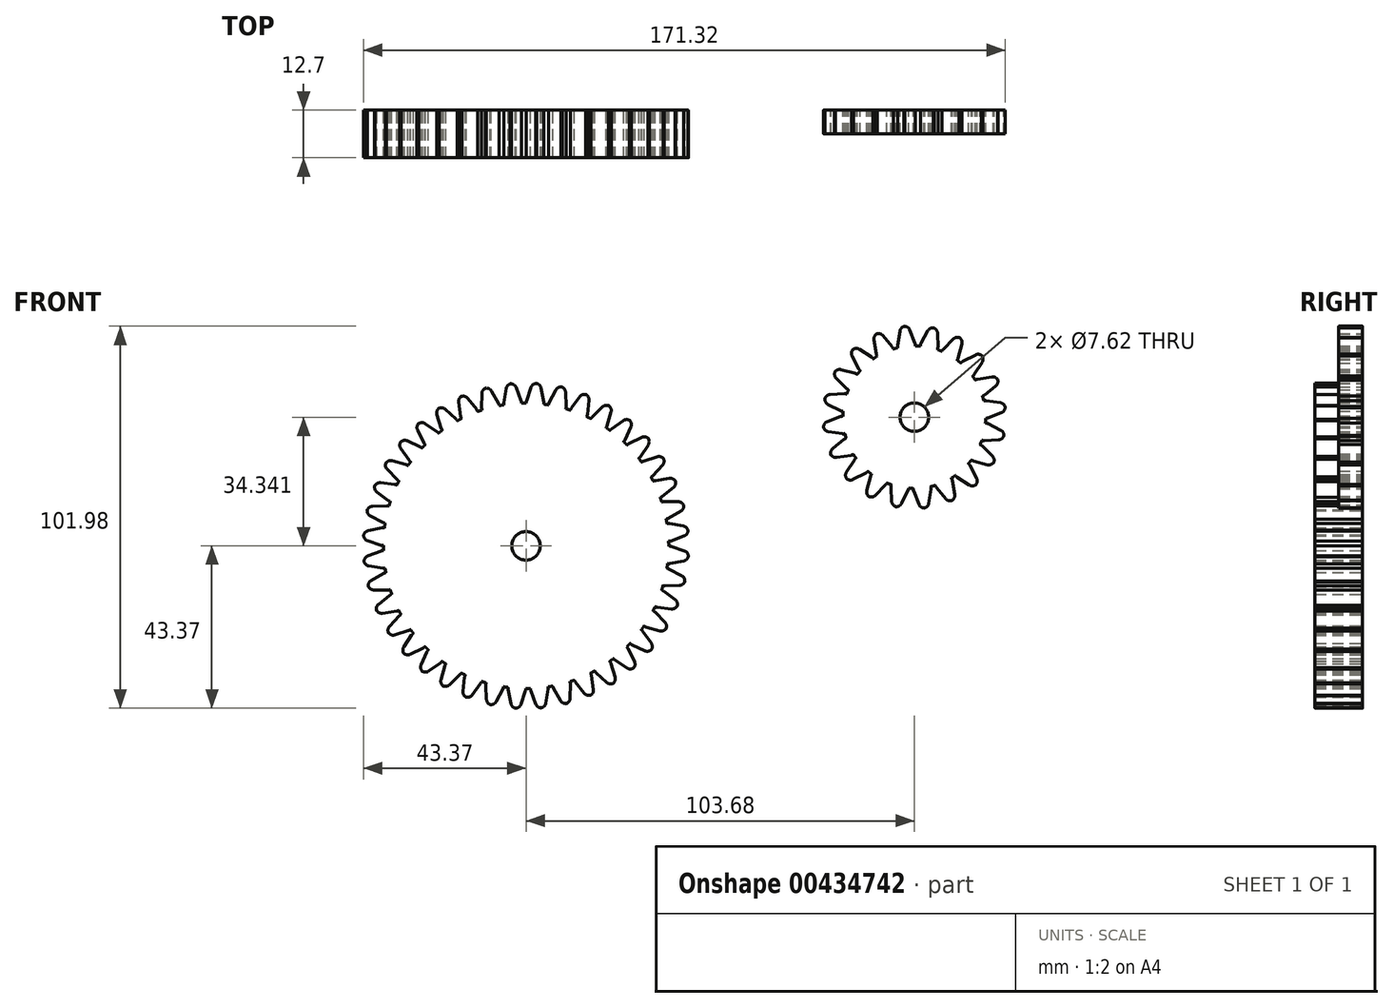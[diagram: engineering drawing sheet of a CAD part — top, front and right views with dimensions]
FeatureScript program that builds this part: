
annotation { "Feature Type Name" : "Feature", "Feature Type Description" : "" }
export const myFeature = defineFeature(function(context is Context, id is Id, definition is map)
    precondition{}
    {
        {
            var Q0;
            Q0=qCreatedBy(makeId("Front.planeOp"),FACE);
            var sketch = newSketch(context, id + "F0", { "sketchPlane" : qUnion([Q0])});
            skCircle(sketch, "E0", {"center": v(0, 0) * mm, "radius": 38.1 * mm});
            skCircle(sketch, "E1", {"center": v(103.68, 34.34) * mm, "radius": 19.05 * mm});
            skCircle(sketch, "E2", {"center": v(0, 0) * mm, "radius": 3.81 * mm});
            skCircle(sketch, "E3", {"center": v(103.68, 34.34) * mm, "radius": 3.81 * mm});
            skLineSegment(sketch, "E4.0", {"start": v(29.52, 22.13) * mm, "end": v(32.62, 17.24) * mm, "construction": true});
            skLineSegment(sketch, "E4.1", {"start": v(32.62, 17.24) * mm, "end": v(34.91, 11.93) * mm, "construction": true});
            skLineSegment(sketch, "E4.2", {"start": v(34.91, 11.93) * mm, "end": v(36.35, 6.32) * mm, "construction": true});
            skLineSegment(sketch, "E4.3", {"start": v(36.35, 6.32) * mm, "end": v(36.89, 0.56) * mm, "construction": true});
            skLineSegment(sketch, "E4.4", {"start": v(36.89, 0.56) * mm, "end": v(36.52, -5.22) * mm, "construction": true});
            skLineSegment(sketch, "E4.5", {"start": v(36.52, -5.22) * mm, "end": v(35.26, -10.87) * mm, "construction": true});
            skLineSegment(sketch, "E4.6", {"start": v(35.26, -10.87) * mm, "end": v(33.12, -16.25) * mm, "construction": true});
            skLineSegment(sketch, "E4.7", {"start": v(33.12, -16.25) * mm, "end": v(30.17, -21.23) * mm, "construction": true});
            skLineSegment(sketch, "E4.8", {"start": v(30.17, -21.23) * mm, "end": v(26.48, -25.7) * mm, "construction": true});
            skLineSegment(sketch, "E4.9", {"start": v(26.48, -25.7) * mm, "end": v(22.13, -29.52) * mm, "construction": true});
            skLineSegment(sketch, "E4.10", {"start": v(22.13, -29.52) * mm, "end": v(17.24, -32.62) * mm, "construction": true});
            skLineSegment(sketch, "E4.11", {"start": v(17.24, -32.62) * mm, "end": v(11.93, -34.91) * mm, "construction": true});
            skLineSegment(sketch, "E4.12", {"start": v(11.93, -34.91) * mm, "end": v(6.32, -36.35) * mm, "construction": true});
            skLineSegment(sketch, "E4.13", {"start": v(6.32, -36.35) * mm, "end": v(0.56, -36.89) * mm, "construction": true});
            skLineSegment(sketch, "E4.14", {"start": v(0.56, -36.89) * mm, "end": v(-5.22, -36.52) * mm, "construction": true});
            skLineSegment(sketch, "E4.15", {"start": v(-5.22, -36.52) * mm, "end": v(-10.87, -35.26) * mm, "construction": true});
            skLineSegment(sketch, "E4.16", {"start": v(-10.87, -35.26) * mm, "end": v(-16.25, -33.12) * mm, "construction": true});
            skLineSegment(sketch, "E4.17", {"start": v(-16.25, -33.12) * mm, "end": v(-21.23, -30.17) * mm, "construction": true});
            skLineSegment(sketch, "E4.18", {"start": v(-21.23, -30.17) * mm, "end": v(-25.7, -26.48) * mm, "construction": true});
            skLineSegment(sketch, "E4.19", {"start": v(-25.7, -26.48) * mm, "end": v(-29.52, -22.13) * mm, "construction": true});
            skLineSegment(sketch, "E4.20", {"start": v(-29.52, -22.13) * mm, "end": v(-32.62, -17.24) * mm, "construction": true});
            skLineSegment(sketch, "E4.21", {"start": v(-32.62, -17.24) * mm, "end": v(-34.91, -11.93) * mm, "construction": true});
            skLineSegment(sketch, "E4.22", {"start": v(-34.91, -11.93) * mm, "end": v(-36.35, -6.32) * mm, "construction": true});
            skLineSegment(sketch, "E4.23", {"start": v(-36.35, -6.32) * mm, "end": v(-36.89, -0.56) * mm, "construction": true});
            skLineSegment(sketch, "E4.24", {"start": v(-36.89, -0.56) * mm, "end": v(-36.52, 5.22) * mm, "construction": true});
            skLineSegment(sketch, "E4.25", {"start": v(-36.52, 5.22) * mm, "end": v(-35.26, 10.87) * mm, "construction": true});
            skLineSegment(sketch, "E4.26", {"start": v(-35.26, 10.87) * mm, "end": v(-33.12, 16.25) * mm, "construction": true});
            skLineSegment(sketch, "E4.27", {"start": v(-33.12, 16.25) * mm, "end": v(-30.17, 21.23) * mm, "construction": true});
            skLineSegment(sketch, "E4.28", {"start": v(-30.17, 21.23) * mm, "end": v(-26.48, 25.7) * mm, "construction": true});
            skLineSegment(sketch, "E4.29", {"start": v(-26.48, 25.7) * mm, "end": v(-22.13, 29.52) * mm, "construction": true});
            skLineSegment(sketch, "E4.30", {"start": v(-22.13, 29.52) * mm, "end": v(-17.24, 32.62) * mm, "construction": true});
            skLineSegment(sketch, "E4.31", {"start": v(-17.24, 32.62) * mm, "end": v(-11.93, 34.91) * mm, "construction": true});
            skLineSegment(sketch, "E4.32", {"start": v(-11.93, 34.91) * mm, "end": v(-6.32, 36.35) * mm, "construction": true});
            skLineSegment(sketch, "E4.33", {"start": v(-6.32, 36.35) * mm, "end": v(-0.56, 36.89) * mm, "construction": true});
            skLineSegment(sketch, "E4.34", {"start": v(-0.56, 36.89) * mm, "end": v(5.22, 36.52) * mm, "construction": true});
            skLineSegment(sketch, "E4.35", {"start": v(5.22, 36.52) * mm, "end": v(10.87, 35.26) * mm, "construction": true});
            skLineSegment(sketch, "E4.36", {"start": v(10.87, 35.26) * mm, "end": v(16.25, 33.12) * mm, "construction": true});
            skLineSegment(sketch, "E4.37", {"start": v(16.25, 33.12) * mm, "end": v(21.23, 30.17) * mm, "construction": true});
            skLineSegment(sketch, "E4.38", {"start": v(21.23, 30.17) * mm, "end": v(25.7, 26.48) * mm, "construction": true});
            skLineSegment(sketch, "E4.39", {"start": v(25.7, 26.48) * mm, "end": v(29.52, 22.13) * mm, "construction": true});
            skLineSegment(sketch, "E5", {"start": v(-17.36, 39.83) * mm, "end": v(-17.1, 39.94) * mm});
            skLineSegment(sketch, "E6", {"start": v(-15.56, 39.37) * mm, "end": v(-13.2, 36.38) * mm});
            skLineSegment(sketch, "E7", {"start": v(-13.77, 34.12) * mm, "end": v(-15.4, 33.41) * mm});
            skLineSegment(sketch, "E8", {"start": v(-17.45, 34.55) * mm, "end": v(-18, 38.32) * mm});
            skArc(sketch, "E9.filletArc", {"start": v(-17.1, 39.94) * mm, "mid": v(-17.82, 39.28) * mm, "end": v(-18, 38.32) * mm});
            skArc(sketch, "E10.filletArc", {"start": v(-15.56, 39.37) * mm, "mid": v(-16.39, 39.9) * mm, "end": v(-17.36, 39.83) * mm});
            skArc(sketch, "E11.filletArc", {"start": v(-13.77, 34.12) * mm, "mid": v(-12.92, 35.1) * mm, "end": v(-13.2, 36.38) * mm});
            skArc(sketch, "E12.filletArc", {"start": v(-17.45, 34.55) * mm, "mid": v(-16.7, 33.48) * mm, "end": v(-15.4, 33.41) * mm});
            skPoint(sketch, "E13", {"position": v(-14.59, 33.76) * mm});
            skLineSegment(sketch, "E14", {"start": v(-85, 50.08) * mm, "end": v(-84.77, 50.25) * mm});
            skLineSegment(sketch, "E15", {"start": v(-83.15, 50) * mm, "end": v(-80.23, 47.57) * mm});
            skLineSegment(sketch, "E16", {"start": v(-80.32, 45.23) * mm, "end": v(-81.77, 44.2) * mm});
            skLineSegment(sketch, "E17", {"start": v(-84, 44.9) * mm, "end": v(-85.32, 48.48) * mm});
            skArc(sketch, "E18.filletArc", {"start": v(-84.77, 50.25) * mm, "mid": v(-85.35, 49.46) * mm, "end": v(-85.32, 48.48) * mm});
            skArc(sketch, "E19.filletArc", {"start": v(-83.15, 50) * mm, "mid": v(-84.07, 50.36) * mm, "end": v(-85, 50.08) * mm});
            skArc(sketch, "E20.filletArc", {"start": v(-80.32, 45.23) * mm, "mid": v(-79.7, 46.38) * mm, "end": v(-80.23, 47.57) * mm});
            skArc(sketch, "E21.filletArc", {"start": v(-84, 44.9) * mm, "mid": v(-83.06, 44) * mm, "end": v(-81.77, 44.2) * mm});
            skPoint(sketch, "E22", {"position": v(-81.05, 44.72) * mm});
            skLineSegment(sketch, "E23", {"start": v(-94.33, 43.84) * mm, "end": v(-94.02, 44.02) * mm});
            skLineSegment(sketch, "E24", {"start": v(-92.1, 43.68) * mm, "end": v(-89.63, 40.77) * mm});
            skLineSegment(sketch, "E25", {"start": v(-90.02, 38.55) * mm, "end": v(-91.55, 37.65) * mm});
            skLineSegment(sketch, "E26", {"start": v(-93.68, 38.42) * mm, "end": v(-95, 42) * mm});
            skArc(sketch, "E27.filletArc", {"start": v(-94.33, 43.84) * mm, "mid": v(-95, 43.04) * mm, "end": v(-95, 42) * mm});
            skArc(sketch, "E28.filletArc", {"start": v(-92.1, 43.68) * mm, "mid": v(-93, 44.2) * mm, "end": v(-94.02, 44.02) * mm});
            skArc(sketch, "E29.filletArc", {"start": v(-90.02, 38.55) * mm, "mid": v(-89.3, 39.57) * mm, "end": v(-89.63, 40.77) * mm});
            skArc(sketch, "E30.filletArc", {"start": v(-93.68, 38.42) * mm, "mid": v(-92.8, 37.54) * mm, "end": v(-91.55, 37.65) * mm});
            skPoint(sketch, "E31", {"position": v(-90.78, 38.1) * mm});
            skLineSegment(sketch, "E32", {"start": v(-10.92, 42.05) * mm, "end": v(-10.64, 42.12) * mm});
            skLineSegment(sketch, "E33", {"start": v(-9.21, 41.32) * mm, "end": v(-7.34, 38) * mm});
            skLineSegment(sketch, "E34", {"start": v(-8.26, 35.85) * mm, "end": v(-9.99, 35.4) * mm});
            skLineSegment(sketch, "E35", {"start": v(-11.83, 36.85) * mm, "end": v(-11.78, 40.66) * mm});
            skArc(sketch, "E36.filletArc", {"start": v(-10.64, 42.12) * mm, "mid": v(-11.46, 41.59) * mm, "end": v(-11.78, 40.66) * mm});
            skArc(sketch, "E37.filletArc", {"start": v(-9.21, 41.32) * mm, "mid": v(-9.94, 41.98) * mm, "end": v(-10.92, 42.05) * mm});
            skArc(sketch, "E38.filletArc", {"start": v(-8.26, 35.85) * mm, "mid": v(-7.27, 36.7) * mm, "end": v(-7.34, 38) * mm});
            skArc(sketch, "E39.filletArc", {"start": v(-11.83, 36.85) * mm, "mid": v(-11.26, 35.68) * mm, "end": v(-9.99, 35.4) * mm});
            skPoint(sketch, "E40", {"position": v(-9.12, 35.63) * mm});
            skLineSegment(sketch, "E41", {"start": v(-4.2, 43.24) * mm, "end": v(-3.92, 43.27) * mm});
            skLineSegment(sketch, "E42", {"start": v(-2.63, 42.25) * mm, "end": v(-1.3, 38.68) * mm});
            skLineSegment(sketch, "E43", {"start": v(-2.55, 36.7) * mm, "end": v(-4.32, 36.54) * mm});
            skLineSegment(sketch, "E44", {"start": v(-5.91, 38.25) * mm, "end": v(-5.28, 42) * mm});
            skArc(sketch, "E45.filletArc", {"start": v(-3.92, 43.27) * mm, "mid": v(-4.81, 42.87) * mm, "end": v(-5.28, 42) * mm});
            skArc(sketch, "E46.filletArc", {"start": v(-2.63, 42.25) * mm, "mid": v(-3.25, 43.01) * mm, "end": v(-4.2, 43.24) * mm});
            skArc(sketch, "E47.filletArc", {"start": v(-2.55, 36.7) * mm, "mid": v(-1.44, 37.38) * mm, "end": v(-1.3, 38.68) * mm});
            skArc(sketch, "E48.filletArc", {"start": v(-5.91, 38.25) * mm, "mid": v(-5.54, 37) * mm, "end": v(-4.32, 36.54) * mm});
            skPoint(sketch, "E49", {"position": v(-3.44, 36.62) * mm});
            skLineSegment(sketch, "E50", {"start": v(2.61, 43.37) * mm, "end": v(2.9, 43.35) * mm});
            skLineSegment(sketch, "E51", {"start": v(4, 42.15) * mm, "end": v(4.76, 38.41) * mm});
            skLineSegment(sketch, "E52", {"start": v(3.22, 36.65) * mm, "end": v(1.45, 36.76) * mm});
            skLineSegment(sketch, "E53", {"start": v(0.14, 38.7) * mm, "end": v(1.36, 42.31) * mm});
            skArc(sketch, "E54.filletArc", {"start": v(2.9, 43.35) * mm, "mid": v(1.95, 43.1) * mm, "end": v(1.36, 42.31) * mm});
            skArc(sketch, "E55.filletArc", {"start": v(4, 42.15) * mm, "mid": v(3.52, 43) * mm, "end": v(2.61, 43.37) * mm});
            skArc(sketch, "E56.filletArc", {"start": v(3.22, 36.65) * mm, "mid": v(4.42, 37.15) * mm, "end": v(4.76, 38.41) * mm});
            skArc(sketch, "E57.filletArc", {"start": v(0.14, 38.7) * mm, "mid": v(0.31, 37.41) * mm, "end": v(1.45, 36.76) * mm});
            skPoint(sketch, "E58", {"position": v(2.33, 36.7) * mm});
            skLineSegment(sketch, "E59", {"start": v(9.36, 42.42) * mm, "end": v(9.65, 42.36) * mm});
            skLineSegment(sketch, "E60", {"start": v(10.55, 41) * mm, "end": v(10.7, 37.2) * mm});
            skLineSegment(sketch, "E61", {"start": v(8.91, 35.7) * mm, "end": v(7.18, 36.08) * mm});
            skLineSegment(sketch, "E62", {"start": v(6.2, 38.2) * mm, "end": v(7.96, 41.58) * mm});
            skArc(sketch, "E63.filletArc", {"start": v(9.65, 42.36) * mm, "mid": v(8.67, 42.26) * mm, "end": v(7.96, 41.58) * mm});
            skArc(sketch, "E64.filletArc", {"start": v(10.55, 41) * mm, "mid": v(10.2, 41.91) * mm, "end": v(9.36, 42.42) * mm});
            skArc(sketch, "E65.filletArc", {"start": v(8.91, 35.7) * mm, "mid": v(10.18, 36) * mm, "end": v(10.7, 37.2) * mm});
            skArc(sketch, "E66.filletArc", {"start": v(6.2, 38.2) * mm, "mid": v(6.16, 36.9) * mm, "end": v(7.18, 36.08) * mm});
            skPoint(sketch, "E67", {"position": v(8.05, 35.89) * mm});
            skLineSegment(sketch, "E68", {"start": v(15.88, 40.44) * mm, "end": v(16.15, 40.33) * mm});
            skLineSegment(sketch, "E69", {"start": v(16.84, 38.84) * mm, "end": v(16.4, 35.06) * mm});
            skLineSegment(sketch, "E70", {"start": v(14.39, 33.86) * mm, "end": v(12.73, 34.52) * mm});
            skLineSegment(sketch, "E71", {"start": v(12.1, 36.77) * mm, "end": v(14.37, 39.82) * mm});
            skArc(sketch, "E72.filletArc", {"start": v(16.15, 40.33) * mm, "mid": v(15.17, 40.38) * mm, "end": v(14.37, 39.82) * mm});
            skArc(sketch, "E73.filletArc", {"start": v(16.84, 38.84) * mm, "mid": v(16.63, 39.8) * mm, "end": v(15.88, 40.44) * mm});
            skArc(sketch, "E74.filletArc", {"start": v(14.39, 33.86) * mm, "mid": v(15.69, 33.97) * mm, "end": v(16.4, 35.06) * mm});
            skArc(sketch, "E75.filletArc", {"start": v(12.1, 36.77) * mm, "mid": v(11.86, 35.48) * mm, "end": v(12.73, 34.52) * mm});
            skPoint(sketch, "E76", {"position": v(13.56, 34.19) * mm});
            skLineSegment(sketch, "E77", {"start": v(22.01, 37.45) * mm, "end": v(22.26, 37.3) * mm});
            skLineSegment(sketch, "E78", {"start": v(22.7, 35.73) * mm, "end": v(21.68, 32.06) * mm});
            skLineSegment(sketch, "E79", {"start": v(19.5, 31.2) * mm, "end": v(17.98, 32.1) * mm});
            skLineSegment(sketch, "E80", {"start": v(17.7, 34.42) * mm, "end": v(20.42, 37.09) * mm});
            skArc(sketch, "E81.filletArc", {"start": v(22.26, 37.3) * mm, "mid": v(21.3, 37.5) * mm, "end": v(20.42, 37.09) * mm});
            skArc(sketch, "E82.filletArc", {"start": v(22.7, 35.73) * mm, "mid": v(22.65, 36.71) * mm, "end": v(22.01, 37.45) * mm});
            skArc(sketch, "E83.filletArc", {"start": v(19.5, 31.2) * mm, "mid": v(20.8, 31.1) * mm, "end": v(21.68, 32.06) * mm});
            skArc(sketch, "E84.filletArc", {"start": v(17.7, 34.42) * mm, "mid": v(17.26, 33.2) * mm, "end": v(17.98, 32.1) * mm});
            skPoint(sketch, "E85", {"position": v(18.74, 31.65) * mm});
            skLineSegment(sketch, "E86", {"start": v(27.6, 33.55) * mm, "end": v(27.83, 33.36) * mm});
            skLineSegment(sketch, "E87", {"start": v(28.02, 31.74) * mm, "end": v(26.43, 28.28) * mm});
            skLineSegment(sketch, "E88", {"start": v(24.15, 27.76) * mm, "end": v(22.78, 28.9) * mm});
            skLineSegment(sketch, "E89", {"start": v(22.86, 31.23) * mm, "end": v(25.97, 33.43) * mm});
            skArc(sketch, "E90.filletArc", {"start": v(27.83, 33.36) * mm, "mid": v(26.91, 33.71) * mm, "end": v(25.97, 33.43) * mm});
            skArc(sketch, "E91.filletArc", {"start": v(28.02, 31.74) * mm, "mid": v(28.12, 32.72) * mm, "end": v(27.6, 33.55) * mm});
            skArc(sketch, "E92.filletArc", {"start": v(24.15, 27.76) * mm, "mid": v(25.42, 27.46) * mm, "end": v(26.43, 28.28) * mm});
            skArc(sketch, "E93.filletArc", {"start": v(22.86, 31.23) * mm, "mid": v(22.24, 30.08) * mm, "end": v(22.78, 28.9) * mm});
            skPoint(sketch, "E94", {"position": v(23.46, 28.32) * mm});
            skLineSegment(sketch, "E95", {"start": v(32.51, 28.82) * mm, "end": v(32.7, 28.6) * mm});
            skLineSegment(sketch, "E96", {"start": v(32.64, 26.97) * mm, "end": v(30.53, 23.8) * mm});
            skLineSegment(sketch, "E97", {"start": v(28.2, 23.64) * mm, "end": v(27.02, 24.97) * mm});
            skLineSegment(sketch, "E98", {"start": v(27.47, 27.27) * mm, "end": v(30.88, 28.96) * mm});
            skArc(sketch, "E99.filletArc", {"start": v(32.7, 28.6) * mm, "mid": v(31.85, 29.09) * mm, "end": v(30.88, 28.96) * mm});
            skArc(sketch, "E100.filletArc", {"start": v(32.64, 26.97) * mm, "mid": v(32.89, 27.91) * mm, "end": v(32.51, 28.82) * mm});
            skArc(sketch, "E101.filletArc", {"start": v(28.2, 23.64) * mm, "mid": v(29.4, 23.14) * mm, "end": v(30.53, 23.8) * mm});
            skArc(sketch, "E102.filletArc", {"start": v(27.47, 27.27) * mm, "mid": v(26.68, 26.23) * mm, "end": v(27.02, 24.97) * mm});
            skPoint(sketch, "E103", {"position": v(27.6, 24.3) * mm});
            skLineSegment(sketch, "E104", {"start": v(36.62, 23.38) * mm, "end": v(36.77, 23.13) * mm});
            skLineSegment(sketch, "E105", {"start": v(36.45, 21.53) * mm, "end": v(33.87, 18.73) * mm});
            skLineSegment(sketch, "E106", {"start": v(31.54, 18.94) * mm, "end": v(30.6, 20.44) * mm});
            skLineSegment(sketch, "E107", {"start": v(31.4, 22.64) * mm, "end": v(35.03, 23.77) * mm});
            skArc(sketch, "E108.filletArc", {"start": v(36.77, 23.13) * mm, "mid": v(36.01, 23.75) * mm, "end": v(35.03, 23.77) * mm});
            skArc(sketch, "E109.filletArc", {"start": v(36.45, 21.53) * mm, "mid": v(36.85, 22.43) * mm, "end": v(36.62, 23.38) * mm});
            skArc(sketch, "E110.filletArc", {"start": v(31.54, 18.94) * mm, "mid": v(32.66, 18.26) * mm, "end": v(33.87, 18.73) * mm});
            skArc(sketch, "E111.filletArc", {"start": v(31.4, 22.64) * mm, "mid": v(30.45, 21.74) * mm, "end": v(30.6, 20.44) * mm});
            skPoint(sketch, "E112", {"position": v(31.07, 19.69) * mm});
            skLineSegment(sketch, "E113", {"start": v(39.83, 17.36) * mm, "end": v(39.94, 17.1) * mm});
            skLineSegment(sketch, "E114", {"start": v(39.37, 15.56) * mm, "end": v(36.38, 13.2) * mm});
            skLineSegment(sketch, "E115", {"start": v(34.12, 13.77) * mm, "end": v(33.41, 15.4) * mm});
            skLineSegment(sketch, "E116", {"start": v(34.55, 17.45) * mm, "end": v(38.32, 18) * mm});
            skArc(sketch, "E117.filletArc", {"start": v(39.94, 17.1) * mm, "mid": v(39.28, 17.82) * mm, "end": v(38.32, 18) * mm});
            skArc(sketch, "E118.filletArc", {"start": v(39.37, 15.56) * mm, "mid": v(39.9, 16.39) * mm, "end": v(39.83, 17.36) * mm});
            skArc(sketch, "E119.filletArc", {"start": v(34.12, 13.77) * mm, "mid": v(35.1, 12.92) * mm, "end": v(36.38, 13.2) * mm});
            skArc(sketch, "E120.filletArc", {"start": v(34.55, 17.45) * mm, "mid": v(33.48, 16.7) * mm, "end": v(33.41, 15.4) * mm});
            skPoint(sketch, "E121", {"position": v(33.76, 14.59) * mm});
            skLineSegment(sketch, "E122", {"start": v(42.05, 10.92) * mm, "end": v(42.12, 10.64) * mm});
            skLineSegment(sketch, "E123", {"start": v(41.32, 9.21) * mm, "end": v(38, 7.34) * mm});
            skLineSegment(sketch, "E124", {"start": v(35.85, 8.26) * mm, "end": v(35.4, 9.99) * mm});
            skLineSegment(sketch, "E125", {"start": v(36.85, 11.83) * mm, "end": v(40.66, 11.78) * mm});
            skArc(sketch, "E126.filletArc", {"start": v(42.12, 10.64) * mm, "mid": v(41.59, 11.46) * mm, "end": v(40.66, 11.78) * mm});
            skArc(sketch, "E127.filletArc", {"start": v(41.32, 9.21) * mm, "mid": v(41.98, 9.94) * mm, "end": v(42.05, 10.92) * mm});
            skArc(sketch, "E128.filletArc", {"start": v(35.85, 8.26) * mm, "mid": v(36.7, 7.27) * mm, "end": v(38, 7.34) * mm});
            skArc(sketch, "E129.filletArc", {"start": v(36.85, 11.83) * mm, "mid": v(35.68, 11.26) * mm, "end": v(35.4, 9.99) * mm});
            skPoint(sketch, "E130", {"position": v(35.63, 9.12) * mm});
            skLineSegment(sketch, "E131", {"start": v(43.24, 4.2) * mm, "end": v(43.27, 3.92) * mm});
            skLineSegment(sketch, "E132", {"start": v(42.25, 2.63) * mm, "end": v(38.68, 1.3) * mm});
            skLineSegment(sketch, "E133", {"start": v(36.7, 2.55) * mm, "end": v(36.54, 4.32) * mm});
            skLineSegment(sketch, "E134", {"start": v(38.25, 5.91) * mm, "end": v(42, 5.28) * mm});
            skArc(sketch, "E135.filletArc", {"start": v(43.27, 3.92) * mm, "mid": v(42.87, 4.81) * mm, "end": v(42, 5.28) * mm});
            skArc(sketch, "E136.filletArc", {"start": v(42.25, 2.63) * mm, "mid": v(43.01, 3.25) * mm, "end": v(43.24, 4.2) * mm});
            skArc(sketch, "E137.filletArc", {"start": v(36.7, 2.55) * mm, "mid": v(37.38, 1.44) * mm, "end": v(38.68, 1.3) * mm});
            skArc(sketch, "E138.filletArc", {"start": v(38.25, 5.91) * mm, "mid": v(37, 5.54) * mm, "end": v(36.54, 4.32) * mm});
            skPoint(sketch, "E139", {"position": v(36.62, 3.44) * mm});
            skLineSegment(sketch, "E140", {"start": v(43.37, -2.61) * mm, "end": v(43.35, -2.9) * mm});
            skLineSegment(sketch, "E141", {"start": v(42.15, -4) * mm, "end": v(38.41, -4.76) * mm});
            skLineSegment(sketch, "E142", {"start": v(36.65, -3.22) * mm, "end": v(36.76, -1.45) * mm});
            skLineSegment(sketch, "E143", {"start": v(38.7, -0.14) * mm, "end": v(42.31, -1.36) * mm});
            skArc(sketch, "E144.filletArc", {"start": v(43.35, -2.9) * mm, "mid": v(43.1, -1.95) * mm, "end": v(42.31, -1.36) * mm});
            skArc(sketch, "E145.filletArc", {"start": v(42.15, -4) * mm, "mid": v(43, -3.52) * mm, "end": v(43.37, -2.61) * mm});
            skArc(sketch, "E146.filletArc", {"start": v(36.65, -3.22) * mm, "mid": v(37.15, -4.42) * mm, "end": v(38.41, -4.76) * mm});
            skArc(sketch, "E147.filletArc", {"start": v(38.7, -0.14) * mm, "mid": v(37.41, -0.31) * mm, "end": v(36.76, -1.45) * mm});
            skPoint(sketch, "E148", {"position": v(36.7, -2.33) * mm});
            skLineSegment(sketch, "E149", {"start": v(42.42, -9.36) * mm, "end": v(42.36, -9.65) * mm});
            skLineSegment(sketch, "E150", {"start": v(41, -10.55) * mm, "end": v(37.2, -10.7) * mm});
            skLineSegment(sketch, "E151", {"start": v(35.7, -8.91) * mm, "end": v(36.08, -7.18) * mm});
            skLineSegment(sketch, "E152", {"start": v(38.2, -6.2) * mm, "end": v(41.58, -7.96) * mm});
            skArc(sketch, "E153.filletArc", {"start": v(42.36, -9.65) * mm, "mid": v(42.26, -8.67) * mm, "end": v(41.58, -7.96) * mm});
            skArc(sketch, "E154.filletArc", {"start": v(41, -10.55) * mm, "mid": v(41.91, -10.2) * mm, "end": v(42.42, -9.36) * mm});
            skArc(sketch, "E155.filletArc", {"start": v(35.7, -8.91) * mm, "mid": v(36, -10.18) * mm, "end": v(37.2, -10.7) * mm});
            skArc(sketch, "E156.filletArc", {"start": v(38.2, -6.2) * mm, "mid": v(36.9, -6.16) * mm, "end": v(36.08, -7.18) * mm});
            skPoint(sketch, "E157", {"position": v(35.89, -8.05) * mm});
            skLineSegment(sketch, "E158", {"start": v(40.44, -15.88) * mm, "end": v(40.33, -16.15) * mm});
            skLineSegment(sketch, "E159", {"start": v(38.84, -16.84) * mm, "end": v(35.06, -16.4) * mm});
            skLineSegment(sketch, "E160", {"start": v(33.86, -14.39) * mm, "end": v(34.52, -12.73) * mm});
            skLineSegment(sketch, "E161", {"start": v(36.77, -12.1) * mm, "end": v(39.82, -14.37) * mm});
            skArc(sketch, "E162.filletArc", {"start": v(40.33, -16.15) * mm, "mid": v(40.38, -15.17) * mm, "end": v(39.82, -14.37) * mm});
            skArc(sketch, "E163.filletArc", {"start": v(38.84, -16.84) * mm, "mid": v(39.8, -16.63) * mm, "end": v(40.44, -15.88) * mm});
            skArc(sketch, "E164.filletArc", {"start": v(33.86, -14.39) * mm, "mid": v(33.97, -15.69) * mm, "end": v(35.06, -16.4) * mm});
            skArc(sketch, "E165.filletArc", {"start": v(36.77, -12.1) * mm, "mid": v(35.48, -11.86) * mm, "end": v(34.52, -12.73) * mm});
            skPoint(sketch, "E166", {"position": v(34.19, -13.56) * mm});
            skLineSegment(sketch, "E167", {"start": v(37.45, -22.01) * mm, "end": v(37.3, -22.26) * mm});
            skLineSegment(sketch, "E168", {"start": v(35.73, -22.7) * mm, "end": v(32.06, -21.68) * mm});
            skLineSegment(sketch, "E169", {"start": v(31.2, -19.5) * mm, "end": v(32.1, -17.98) * mm});
            skLineSegment(sketch, "E170", {"start": v(34.42, -17.7) * mm, "end": v(37.09, -20.42) * mm});
            skArc(sketch, "E171.filletArc", {"start": v(37.3, -22.26) * mm, "mid": v(37.5, -21.3) * mm, "end": v(37.09, -20.42) * mm});
            skArc(sketch, "E172.filletArc", {"start": v(35.73, -22.7) * mm, "mid": v(36.71, -22.65) * mm, "end": v(37.45, -22.01) * mm});
            skArc(sketch, "E173.filletArc", {"start": v(31.2, -19.5) * mm, "mid": v(31.1, -20.8) * mm, "end": v(32.06, -21.68) * mm});
            skArc(sketch, "E174.filletArc", {"start": v(34.42, -17.7) * mm, "mid": v(33.2, -17.26) * mm, "end": v(32.1, -17.98) * mm});
            skPoint(sketch, "E175", {"position": v(31.65, -18.74) * mm});
            skLineSegment(sketch, "E176", {"start": v(33.55, -27.6) * mm, "end": v(33.36, -27.83) * mm});
            skLineSegment(sketch, "E177", {"start": v(31.74, -28.02) * mm, "end": v(28.28, -26.43) * mm});
            skLineSegment(sketch, "E178", {"start": v(27.76, -24.15) * mm, "end": v(28.9, -22.78) * mm});
            skLineSegment(sketch, "E179", {"start": v(31.23, -22.86) * mm, "end": v(33.43, -25.97) * mm});
            skArc(sketch, "E180.filletArc", {"start": v(33.36, -27.83) * mm, "mid": v(33.71, -26.91) * mm, "end": v(33.43, -25.97) * mm});
            skArc(sketch, "E181.filletArc", {"start": v(31.74, -28.02) * mm, "mid": v(32.72, -28.12) * mm, "end": v(33.55, -27.6) * mm});
            skArc(sketch, "E182.filletArc", {"start": v(27.76, -24.15) * mm, "mid": v(27.46, -25.42) * mm, "end": v(28.28, -26.43) * mm});
            skArc(sketch, "E183.filletArc", {"start": v(31.23, -22.86) * mm, "mid": v(30.08, -22.24) * mm, "end": v(28.9, -22.78) * mm});
            skPoint(sketch, "E184", {"position": v(28.32, -23.46) * mm});
            skLineSegment(sketch, "E185", {"start": v(28.82, -32.51) * mm, "end": v(28.6, -32.7) * mm});
            skLineSegment(sketch, "E186", {"start": v(26.97, -32.64) * mm, "end": v(23.8, -30.53) * mm});
            skLineSegment(sketch, "E187", {"start": v(23.64, -28.2) * mm, "end": v(24.97, -27.02) * mm});
            skLineSegment(sketch, "E188", {"start": v(27.27, -27.47) * mm, "end": v(28.96, -30.88) * mm});
            skArc(sketch, "E189.filletArc", {"start": v(28.6, -32.7) * mm, "mid": v(29.09, -31.85) * mm, "end": v(28.96, -30.88) * mm});
            skArc(sketch, "E190.filletArc", {"start": v(26.97, -32.64) * mm, "mid": v(27.91, -32.89) * mm, "end": v(28.82, -32.51) * mm});
            skArc(sketch, "E191.filletArc", {"start": v(23.64, -28.2) * mm, "mid": v(23.14, -29.4) * mm, "end": v(23.8, -30.53) * mm});
            skArc(sketch, "E192.filletArc", {"start": v(27.27, -27.47) * mm, "mid": v(26.23, -26.68) * mm, "end": v(24.97, -27.02) * mm});
            skPoint(sketch, "E193", {"position": v(24.3, -27.6) * mm});
            skLineSegment(sketch, "E194", {"start": v(23.38, -36.62) * mm, "end": v(23.13, -36.77) * mm});
            skLineSegment(sketch, "E195", {"start": v(21.53, -36.45) * mm, "end": v(18.73, -33.87) * mm});
            skLineSegment(sketch, "E196", {"start": v(18.94, -31.54) * mm, "end": v(20.44, -30.6) * mm});
            skLineSegment(sketch, "E197", {"start": v(22.64, -31.4) * mm, "end": v(23.77, -35.03) * mm});
            skArc(sketch, "E198.filletArc", {"start": v(23.13, -36.77) * mm, "mid": v(23.75, -36.01) * mm, "end": v(23.77, -35.03) * mm});
            skArc(sketch, "E199.filletArc", {"start": v(21.53, -36.45) * mm, "mid": v(22.43, -36.85) * mm, "end": v(23.38, -36.62) * mm});
            skArc(sketch, "E200.filletArc", {"start": v(18.94, -31.54) * mm, "mid": v(18.26, -32.66) * mm, "end": v(18.73, -33.87) * mm});
            skArc(sketch, "E201.filletArc", {"start": v(22.64, -31.4) * mm, "mid": v(21.74, -30.45) * mm, "end": v(20.44, -30.6) * mm});
            skPoint(sketch, "E202", {"position": v(19.69, -31.07) * mm});
            skLineSegment(sketch, "E203", {"start": v(4.2, -43.24) * mm, "end": v(3.92, -43.27) * mm});
            skLineSegment(sketch, "E204", {"start": v(2.63, -42.25) * mm, "end": v(1.3, -38.68) * mm});
            skLineSegment(sketch, "E205", {"start": v(2.55, -36.7) * mm, "end": v(4.32, -36.54) * mm});
            skLineSegment(sketch, "E206", {"start": v(5.91, -38.25) * mm, "end": v(5.28, -42) * mm});
            skArc(sketch, "E207.filletArc", {"start": v(3.92, -43.27) * mm, "mid": v(4.81, -42.87) * mm, "end": v(5.28, -42) * mm});
            skArc(sketch, "E208.filletArc", {"start": v(2.63, -42.25) * mm, "mid": v(3.25, -43.01) * mm, "end": v(4.2, -43.24) * mm});
            skArc(sketch, "E209.filletArc", {"start": v(2.55, -36.7) * mm, "mid": v(1.44, -37.38) * mm, "end": v(1.3, -38.68) * mm});
            skArc(sketch, "E210.filletArc", {"start": v(5.91, -38.25) * mm, "mid": v(5.54, -37) * mm, "end": v(4.32, -36.54) * mm});
            skPoint(sketch, "E211", {"position": v(3.44, -36.62) * mm});
            skLineSegment(sketch, "E212", {"start": v(10.92, -42.05) * mm, "end": v(10.64, -42.12) * mm});
            skLineSegment(sketch, "E213", {"start": v(9.21, -41.32) * mm, "end": v(7.34, -38) * mm});
            skLineSegment(sketch, "E214", {"start": v(8.26, -35.85) * mm, "end": v(9.99, -35.4) * mm});
            skLineSegment(sketch, "E215", {"start": v(11.83, -36.85) * mm, "end": v(11.78, -40.66) * mm});
            skArc(sketch, "E216.filletArc", {"start": v(10.64, -42.12) * mm, "mid": v(11.46, -41.59) * mm, "end": v(11.78, -40.66) * mm});
            skArc(sketch, "E217.filletArc", {"start": v(9.21, -41.32) * mm, "mid": v(9.94, -41.98) * mm, "end": v(10.92, -42.05) * mm});
            skArc(sketch, "E218.filletArc", {"start": v(8.26, -35.85) * mm, "mid": v(7.27, -36.7) * mm, "end": v(7.34, -38) * mm});
            skArc(sketch, "E219.filletArc", {"start": v(11.83, -36.85) * mm, "mid": v(11.26, -35.68) * mm, "end": v(9.99, -35.4) * mm});
            skPoint(sketch, "E220", {"position": v(9.12, -35.63) * mm});
            skLineSegment(sketch, "E221", {"start": v(17.36, -39.83) * mm, "end": v(17.1, -39.94) * mm});
            skLineSegment(sketch, "E222", {"start": v(15.56, -39.37) * mm, "end": v(13.2, -36.38) * mm});
            skLineSegment(sketch, "E223", {"start": v(13.77, -34.12) * mm, "end": v(15.4, -33.41) * mm});
            skLineSegment(sketch, "E224", {"start": v(17.45, -34.55) * mm, "end": v(18, -38.32) * mm});
            skArc(sketch, "E225.filletArc", {"start": v(17.1, -39.94) * mm, "mid": v(17.82, -39.28) * mm, "end": v(18, -38.32) * mm});
            skArc(sketch, "E226.filletArc", {"start": v(15.56, -39.37) * mm, "mid": v(16.39, -39.9) * mm, "end": v(17.36, -39.83) * mm});
            skArc(sketch, "E227.filletArc", {"start": v(13.77, -34.12) * mm, "mid": v(12.92, -35.1) * mm, "end": v(13.2, -36.38) * mm});
            skArc(sketch, "E228.filletArc", {"start": v(17.45, -34.55) * mm, "mid": v(16.7, -33.48) * mm, "end": v(15.4, -33.41) * mm});
            skPoint(sketch, "E229", {"position": v(14.59, -33.76) * mm});
            skLineSegment(sketch, "E230", {"start": v(-2.61, -43.37) * mm, "end": v(-2.9, -43.35) * mm});
            skLineSegment(sketch, "E231", {"start": v(-4, -42.15) * mm, "end": v(-4.76, -38.41) * mm});
            skLineSegment(sketch, "E232", {"start": v(-3.22, -36.65) * mm, "end": v(-1.45, -36.76) * mm});
            skLineSegment(sketch, "E233", {"start": v(-0.14, -38.7) * mm, "end": v(-1.36, -42.31) * mm});
            skArc(sketch, "E234.filletArc", {"start": v(-2.9, -43.35) * mm, "mid": v(-1.95, -43.1) * mm, "end": v(-1.36, -42.31) * mm});
            skArc(sketch, "E235.filletArc", {"start": v(-4, -42.15) * mm, "mid": v(-3.52, -43) * mm, "end": v(-2.61, -43.37) * mm});
            skArc(sketch, "E236.filletArc", {"start": v(-3.22, -36.65) * mm, "mid": v(-4.42, -37.15) * mm, "end": v(-4.76, -38.41) * mm});
            skArc(sketch, "E237.filletArc", {"start": v(-0.14, -38.7) * mm, "mid": v(-0.31, -37.41) * mm, "end": v(-1.45, -36.76) * mm});
            skPoint(sketch, "E238", {"position": v(-2.33, -36.7) * mm});
            skLineSegment(sketch, "E239", {"start": v(-9.36, -42.42) * mm, "end": v(-9.65, -42.36) * mm});
            skLineSegment(sketch, "E240", {"start": v(-10.55, -41) * mm, "end": v(-10.7, -37.2) * mm});
            skLineSegment(sketch, "E241", {"start": v(-8.91, -35.7) * mm, "end": v(-7.18, -36.08) * mm});
            skLineSegment(sketch, "E242", {"start": v(-6.2, -38.2) * mm, "end": v(-7.96, -41.58) * mm});
            skArc(sketch, "E243.filletArc", {"start": v(-9.65, -42.36) * mm, "mid": v(-8.67, -42.26) * mm, "end": v(-7.96, -41.58) * mm});
            skArc(sketch, "E244.filletArc", {"start": v(-10.55, -41) * mm, "mid": v(-10.2, -41.91) * mm, "end": v(-9.36, -42.42) * mm});
            skArc(sketch, "E245.filletArc", {"start": v(-8.91, -35.7) * mm, "mid": v(-10.18, -36) * mm, "end": v(-10.7, -37.2) * mm});
            skArc(sketch, "E246.filletArc", {"start": v(-6.2, -38.2) * mm, "mid": v(-6.16, -36.9) * mm, "end": v(-7.18, -36.08) * mm});
            skPoint(sketch, "E247", {"position": v(-8.05, -35.89) * mm});
            skLineSegment(sketch, "E248", {"start": v(-15.88, -40.44) * mm, "end": v(-16.15, -40.33) * mm});
            skLineSegment(sketch, "E249", {"start": v(-16.84, -38.84) * mm, "end": v(-16.4, -35.06) * mm});
            skLineSegment(sketch, "E250", {"start": v(-14.39, -33.86) * mm, "end": v(-12.73, -34.52) * mm});
            skLineSegment(sketch, "E251", {"start": v(-12.1, -36.77) * mm, "end": v(-14.37, -39.82) * mm});
            skArc(sketch, "E252.filletArc", {"start": v(-16.15, -40.33) * mm, "mid": v(-15.17, -40.38) * mm, "end": v(-14.37, -39.82) * mm});
            skArc(sketch, "E253.filletArc", {"start": v(-16.84, -38.84) * mm, "mid": v(-16.63, -39.8) * mm, "end": v(-15.88, -40.44) * mm});
            skArc(sketch, "E254.filletArc", {"start": v(-14.39, -33.86) * mm, "mid": v(-15.69, -33.97) * mm, "end": v(-16.4, -35.06) * mm});
            skArc(sketch, "E255.filletArc", {"start": v(-12.1, -36.77) * mm, "mid": v(-11.86, -35.48) * mm, "end": v(-12.73, -34.52) * mm});
            skPoint(sketch, "E256", {"position": v(-13.56, -34.19) * mm});
            skLineSegment(sketch, "E257", {"start": v(-22.01, -37.45) * mm, "end": v(-22.26, -37.3) * mm});
            skLineSegment(sketch, "E258", {"start": v(-22.7, -35.73) * mm, "end": v(-21.68, -32.06) * mm});
            skLineSegment(sketch, "E259", {"start": v(-19.5, -31.2) * mm, "end": v(-17.98, -32.1) * mm});
            skLineSegment(sketch, "E260", {"start": v(-17.7, -34.42) * mm, "end": v(-20.42, -37.09) * mm});
            skArc(sketch, "E261.filletArc", {"start": v(-22.26, -37.3) * mm, "mid": v(-21.3, -37.5) * mm, "end": v(-20.42, -37.09) * mm});
            skArc(sketch, "E262.filletArc", {"start": v(-22.7, -35.73) * mm, "mid": v(-22.65, -36.71) * mm, "end": v(-22.01, -37.45) * mm});
            skArc(sketch, "E263.filletArc", {"start": v(-19.5, -31.2) * mm, "mid": v(-20.8, -31.1) * mm, "end": v(-21.68, -32.06) * mm});
            skArc(sketch, "E264.filletArc", {"start": v(-17.7, -34.42) * mm, "mid": v(-17.26, -33.2) * mm, "end": v(-17.98, -32.1) * mm});
            skPoint(sketch, "E265", {"position": v(-18.74, -31.65) * mm});
            skLineSegment(sketch, "E266", {"start": v(-27.6, -33.55) * mm, "end": v(-27.83, -33.36) * mm});
            skLineSegment(sketch, "E267", {"start": v(-28.02, -31.74) * mm, "end": v(-26.43, -28.28) * mm});
            skLineSegment(sketch, "E268", {"start": v(-24.15, -27.76) * mm, "end": v(-22.78, -28.9) * mm});
            skLineSegment(sketch, "E269", {"start": v(-22.86, -31.23) * mm, "end": v(-25.97, -33.43) * mm});
            skArc(sketch, "E270.filletArc", {"start": v(-27.83, -33.36) * mm, "mid": v(-26.91, -33.71) * mm, "end": v(-25.97, -33.43) * mm});
            skArc(sketch, "E271.filletArc", {"start": v(-28.02, -31.74) * mm, "mid": v(-28.12, -32.72) * mm, "end": v(-27.6, -33.55) * mm});
            skArc(sketch, "E272.filletArc", {"start": v(-24.15, -27.76) * mm, "mid": v(-25.42, -27.46) * mm, "end": v(-26.43, -28.28) * mm});
            skArc(sketch, "E273.filletArc", {"start": v(-22.86, -31.23) * mm, "mid": v(-22.24, -30.08) * mm, "end": v(-22.78, -28.9) * mm});
            skPoint(sketch, "E274", {"position": v(-23.46, -28.32) * mm});
            skLineSegment(sketch, "E275", {"start": v(-32.51, -28.82) * mm, "end": v(-32.7, -28.6) * mm});
            skLineSegment(sketch, "E276", {"start": v(-32.64, -26.97) * mm, "end": v(-30.53, -23.8) * mm});
            skLineSegment(sketch, "E277", {"start": v(-28.2, -23.64) * mm, "end": v(-27.02, -24.97) * mm});
            skLineSegment(sketch, "E278", {"start": v(-27.47, -27.27) * mm, "end": v(-30.88, -28.96) * mm});
            skArc(sketch, "E279.filletArc", {"start": v(-32.7, -28.6) * mm, "mid": v(-31.85, -29.09) * mm, "end": v(-30.88, -28.96) * mm});
            skArc(sketch, "E280.filletArc", {"start": v(-32.64, -26.97) * mm, "mid": v(-32.89, -27.91) * mm, "end": v(-32.51, -28.82) * mm});
            skArc(sketch, "E281.filletArc", {"start": v(-28.2, -23.64) * mm, "mid": v(-29.4, -23.14) * mm, "end": v(-30.53, -23.8) * mm});
            skArc(sketch, "E282.filletArc", {"start": v(-27.47, -27.27) * mm, "mid": v(-26.68, -26.23) * mm, "end": v(-27.02, -24.97) * mm});
            skPoint(sketch, "E283", {"position": v(-27.6, -24.3) * mm});
            skLineSegment(sketch, "E284", {"start": v(-39.83, -17.36) * mm, "end": v(-39.94, -17.1) * mm});
            skLineSegment(sketch, "E285", {"start": v(-39.37, -15.56) * mm, "end": v(-36.38, -13.2) * mm});
            skLineSegment(sketch, "E286", {"start": v(-34.12, -13.77) * mm, "end": v(-33.41, -15.4) * mm});
            skLineSegment(sketch, "E287", {"start": v(-34.55, -17.45) * mm, "end": v(-38.32, -18) * mm});
            skArc(sketch, "E288.filletArc", {"start": v(-39.94, -17.1) * mm, "mid": v(-39.28, -17.82) * mm, "end": v(-38.32, -18) * mm});
            skArc(sketch, "E289.filletArc", {"start": v(-39.37, -15.56) * mm, "mid": v(-39.9, -16.39) * mm, "end": v(-39.83, -17.36) * mm});
            skArc(sketch, "E290.filletArc", {"start": v(-34.12, -13.77) * mm, "mid": v(-35.1, -12.92) * mm, "end": v(-36.38, -13.2) * mm});
            skArc(sketch, "E291.filletArc", {"start": v(-34.55, -17.45) * mm, "mid": v(-33.48, -16.7) * mm, "end": v(-33.41, -15.4) * mm});
            skPoint(sketch, "E292", {"position": v(-33.76, -14.59) * mm});
            skLineSegment(sketch, "E293", {"start": v(-43.23, -4.32) * mm, "end": v(-43.26, -4.03) * mm});
            skLineSegment(sketch, "E294", {"start": v(-42.27, -2.73) * mm, "end": v(-38.72, -1.34) * mm});
            skLineSegment(sketch, "E295", {"start": v(-36.72, -2.55) * mm, "end": v(-36.52, -4.32) * mm});
            skLineSegment(sketch, "E296", {"start": v(-38.2, -5.94) * mm, "end": v(-41.97, -5.37) * mm});
            skArc(sketch, "E297.filletArc", {"start": v(-43.26, -4.03) * mm, "mid": v(-42.84, -4.92) * mm, "end": v(-41.97, -5.37) * mm});
            skArc(sketch, "E298.filletArc", {"start": v(-42.27, -2.73) * mm, "mid": v(-43.02, -3.36) * mm, "end": v(-43.23, -4.32) * mm});
            skArc(sketch, "E299.filletArc", {"start": v(-36.72, -2.55) * mm, "mid": v(-37.42, -1.46) * mm, "end": v(-38.72, -1.34) * mm});
            skArc(sketch, "E300.filletArc", {"start": v(-38.2, -5.94) * mm, "mid": v(-36.96, -5.55) * mm, "end": v(-36.52, -4.32) * mm});
            skPoint(sketch, "E301", {"position": v(-36.62, -3.44) * mm});
            skLineSegment(sketch, "E302", {"start": v(-42.05, -10.92) * mm, "end": v(-42.12, -10.64) * mm});
            skLineSegment(sketch, "E303", {"start": v(-41.32, -9.21) * mm, "end": v(-38, -7.34) * mm});
            skLineSegment(sketch, "E304", {"start": v(-35.85, -8.26) * mm, "end": v(-35.4, -9.99) * mm});
            skLineSegment(sketch, "E305", {"start": v(-36.85, -11.83) * mm, "end": v(-40.66, -11.78) * mm});
            skArc(sketch, "E306.filletArc", {"start": v(-42.12, -10.64) * mm, "mid": v(-41.59, -11.46) * mm, "end": v(-40.66, -11.78) * mm});
            skArc(sketch, "E307.filletArc", {"start": v(-41.32, -9.21) * mm, "mid": v(-41.98, -9.94) * mm, "end": v(-42.05, -10.92) * mm});
            skArc(sketch, "E308.filletArc", {"start": v(-35.85, -8.26) * mm, "mid": v(-36.7, -7.27) * mm, "end": v(-38, -7.34) * mm});
            skArc(sketch, "E309.filletArc", {"start": v(-36.85, -11.83) * mm, "mid": v(-35.68, -11.26) * mm, "end": v(-35.4, -9.99) * mm});
            skPoint(sketch, "E310", {"position": v(-35.63, -9.12) * mm});
            skLineSegment(sketch, "E311", {"start": v(-36.62, -23.38) * mm, "end": v(-36.77, -23.13) * mm});
            skLineSegment(sketch, "E312", {"start": v(-36.45, -21.53) * mm, "end": v(-33.87, -18.73) * mm});
            skLineSegment(sketch, "E313", {"start": v(-31.54, -18.94) * mm, "end": v(-30.6, -20.44) * mm});
            skLineSegment(sketch, "E314", {"start": v(-31.4, -22.64) * mm, "end": v(-35.03, -23.77) * mm});
            skArc(sketch, "E315.filletArc", {"start": v(-36.77, -23.13) * mm, "mid": v(-36.01, -23.75) * mm, "end": v(-35.03, -23.77) * mm});
            skArc(sketch, "E316.filletArc", {"start": v(-36.45, -21.53) * mm, "mid": v(-36.85, -22.43) * mm, "end": v(-36.62, -23.38) * mm});
            skArc(sketch, "E317.filletArc", {"start": v(-31.54, -18.94) * mm, "mid": v(-32.66, -18.26) * mm, "end": v(-33.87, -18.73) * mm});
            skArc(sketch, "E318.filletArc", {"start": v(-31.4, -22.64) * mm, "mid": v(-30.45, -21.74) * mm, "end": v(-30.6, -20.44) * mm});
            skPoint(sketch, "E319", {"position": v(-31.07, -19.69) * mm});
            skLineSegment(sketch, "E320", {"start": v(-37.45, 22.01) * mm, "end": v(-37.3, 22.26) * mm});
            skLineSegment(sketch, "E321", {"start": v(-35.73, 22.7) * mm, "end": v(-32.06, 21.68) * mm});
            skLineSegment(sketch, "E322", {"start": v(-31.2, 19.5) * mm, "end": v(-32.1, 17.98) * mm});
            skLineSegment(sketch, "E323", {"start": v(-34.42, 17.7) * mm, "end": v(-37.09, 20.42) * mm});
            skArc(sketch, "E324.filletArc", {"start": v(-37.3, 22.26) * mm, "mid": v(-37.5, 21.3) * mm, "end": v(-37.09, 20.42) * mm});
            skArc(sketch, "E325.filletArc", {"start": v(-35.73, 22.7) * mm, "mid": v(-36.71, 22.65) * mm, "end": v(-37.45, 22.01) * mm});
            skArc(sketch, "E326.filletArc", {"start": v(-31.2, 19.5) * mm, "mid": v(-31.1, 20.8) * mm, "end": v(-32.06, 21.68) * mm});
            skArc(sketch, "E327.filletArc", {"start": v(-34.42, 17.7) * mm, "mid": v(-33.2, 17.26) * mm, "end": v(-32.1, 17.98) * mm});
            skPoint(sketch, "E328", {"position": v(-31.65, 18.74) * mm});
            skLineSegment(sketch, "E329", {"start": v(-42.42, 9.36) * mm, "end": v(-42.36, 9.65) * mm});
            skLineSegment(sketch, "E330", {"start": v(-41, 10.55) * mm, "end": v(-37.2, 10.7) * mm});
            skLineSegment(sketch, "E331", {"start": v(-35.7, 8.91) * mm, "end": v(-36.08, 7.18) * mm});
            skLineSegment(sketch, "E332", {"start": v(-38.2, 6.2) * mm, "end": v(-41.58, 7.96) * mm});
            skArc(sketch, "E333.filletArc", {"start": v(-42.36, 9.65) * mm, "mid": v(-42.26, 8.67) * mm, "end": v(-41.58, 7.96) * mm});
            skArc(sketch, "E334.filletArc", {"start": v(-41, 10.55) * mm, "mid": v(-41.91, 10.2) * mm, "end": v(-42.42, 9.36) * mm});
            skArc(sketch, "E335.filletArc", {"start": v(-35.7, 8.91) * mm, "mid": v(-36, 10.18) * mm, "end": v(-37.2, 10.7) * mm});
            skArc(sketch, "E336.filletArc", {"start": v(-38.2, 6.2) * mm, "mid": v(-36.9, 6.16) * mm, "end": v(-36.08, 7.18) * mm});
            skPoint(sketch, "E337", {"position": v(-35.89, 8.05) * mm});
            skLineSegment(sketch, "E338", {"start": v(-28.82, 32.51) * mm, "end": v(-28.6, 32.7) * mm});
            skLineSegment(sketch, "E339", {"start": v(-26.97, 32.64) * mm, "end": v(-23.8, 30.53) * mm});
            skLineSegment(sketch, "E340", {"start": v(-23.64, 28.2) * mm, "end": v(-24.97, 27.02) * mm});
            skLineSegment(sketch, "E341", {"start": v(-27.27, 27.47) * mm, "end": v(-28.96, 30.88) * mm});
            skArc(sketch, "E342.filletArc", {"start": v(-28.6, 32.7) * mm, "mid": v(-29.09, 31.85) * mm, "end": v(-28.96, 30.88) * mm});
            skArc(sketch, "E343.filletArc", {"start": v(-26.97, 32.64) * mm, "mid": v(-27.91, 32.89) * mm, "end": v(-28.82, 32.51) * mm});
            skArc(sketch, "E344.filletArc", {"start": v(-23.64, 28.2) * mm, "mid": v(-23.14, 29.4) * mm, "end": v(-23.8, 30.53) * mm});
            skArc(sketch, "E345.filletArc", {"start": v(-27.27, 27.47) * mm, "mid": v(-26.23, 26.68) * mm, "end": v(-24.97, 27.02) * mm});
            skPoint(sketch, "E346", {"position": v(-24.3, 27.6) * mm});
            skLineSegment(sketch, "E347", {"start": v(-23.38, 36.62) * mm, "end": v(-23.13, 36.77) * mm});
            skLineSegment(sketch, "E348", {"start": v(-21.53, 36.45) * mm, "end": v(-18.73, 33.87) * mm});
            skLineSegment(sketch, "E349", {"start": v(-18.94, 31.54) * mm, "end": v(-20.44, 30.6) * mm});
            skLineSegment(sketch, "E350", {"start": v(-22.64, 31.4) * mm, "end": v(-23.77, 35.03) * mm});
            skArc(sketch, "E351.filletArc", {"start": v(-23.13, 36.77) * mm, "mid": v(-23.75, 36.01) * mm, "end": v(-23.77, 35.03) * mm});
            skArc(sketch, "E352.filletArc", {"start": v(-21.53, 36.45) * mm, "mid": v(-22.43, 36.85) * mm, "end": v(-23.38, 36.62) * mm});
            skArc(sketch, "E353.filletArc", {"start": v(-18.94, 31.54) * mm, "mid": v(-18.26, 32.66) * mm, "end": v(-18.73, 33.87) * mm});
            skArc(sketch, "E354.filletArc", {"start": v(-22.64, 31.4) * mm, "mid": v(-21.74, 30.45) * mm, "end": v(-20.44, 30.6) * mm});
            skPoint(sketch, "E355", {"position": v(-19.69, 31.07) * mm});
            skLineSegment(sketch, "E356", {"start": v(-33.55, 27.6) * mm, "end": v(-33.36, 27.83) * mm});
            skLineSegment(sketch, "E357", {"start": v(-31.74, 28.02) * mm, "end": v(-28.28, 26.43) * mm});
            skLineSegment(sketch, "E358", {"start": v(-27.76, 24.15) * mm, "end": v(-28.9, 22.78) * mm});
            skLineSegment(sketch, "E359", {"start": v(-31.23, 22.86) * mm, "end": v(-33.43, 25.97) * mm});
            skArc(sketch, "E360.filletArc", {"start": v(-33.36, 27.83) * mm, "mid": v(-33.71, 26.91) * mm, "end": v(-33.43, 25.97) * mm});
            skArc(sketch, "E361.filletArc", {"start": v(-31.74, 28.02) * mm, "mid": v(-32.72, 28.12) * mm, "end": v(-33.55, 27.6) * mm});
            skArc(sketch, "E362.filletArc", {"start": v(-27.76, 24.15) * mm, "mid": v(-27.46, 25.42) * mm, "end": v(-28.28, 26.43) * mm});
            skArc(sketch, "E363.filletArc", {"start": v(-31.23, 22.86) * mm, "mid": v(-30.08, 22.24) * mm, "end": v(-28.9, 22.78) * mm});
            skPoint(sketch, "E364", {"position": v(-28.32, 23.46) * mm});
            skLineSegment(sketch, "E365", {"start": v(-40.44, 15.88) * mm, "end": v(-40.33, 16.15) * mm});
            skLineSegment(sketch, "E366", {"start": v(-38.84, 16.84) * mm, "end": v(-35.06, 16.4) * mm});
            skLineSegment(sketch, "E367", {"start": v(-33.86, 14.39) * mm, "end": v(-34.52, 12.73) * mm});
            skLineSegment(sketch, "E368", {"start": v(-36.77, 12.1) * mm, "end": v(-39.82, 14.37) * mm});
            skArc(sketch, "E369.filletArc", {"start": v(-40.33, 16.15) * mm, "mid": v(-40.38, 15.17) * mm, "end": v(-39.82, 14.37) * mm});
            skArc(sketch, "E370.filletArc", {"start": v(-38.84, 16.84) * mm, "mid": v(-39.8, 16.63) * mm, "end": v(-40.44, 15.88) * mm});
            skArc(sketch, "E371.filletArc", {"start": v(-33.86, 14.39) * mm, "mid": v(-33.97, 15.69) * mm, "end": v(-35.06, 16.4) * mm});
            skArc(sketch, "E372.filletArc", {"start": v(-36.77, 12.1) * mm, "mid": v(-35.48, 11.86) * mm, "end": v(-34.52, 12.73) * mm});
            skPoint(sketch, "E373", {"position": v(-34.19, 13.56) * mm});
            skLineSegment(sketch, "E374", {"start": v(-43.37, 2.61) * mm, "end": v(-43.35, 2.9) * mm});
            skLineSegment(sketch, "E375", {"start": v(-42.15, 4) * mm, "end": v(-38.41, 4.76) * mm});
            skLineSegment(sketch, "E376", {"start": v(-36.65, 3.22) * mm, "end": v(-36.76, 1.45) * mm});
            skLineSegment(sketch, "E377", {"start": v(-38.7, 0.14) * mm, "end": v(-42.31, 1.36) * mm});
            skArc(sketch, "E378.filletArc", {"start": v(-43.35, 2.9) * mm, "mid": v(-43.1, 1.95) * mm, "end": v(-42.31, 1.36) * mm});
            skArc(sketch, "E379.filletArc", {"start": v(-42.15, 4) * mm, "mid": v(-43, 3.52) * mm, "end": v(-43.37, 2.61) * mm});
            skArc(sketch, "E380.filletArc", {"start": v(-36.65, 3.22) * mm, "mid": v(-37.15, 4.42) * mm, "end": v(-38.41, 4.76) * mm});
            skArc(sketch, "E381.filletArc", {"start": v(-38.7, 0.14) * mm, "mid": v(-37.41, 0.31) * mm, "end": v(-36.76, 1.45) * mm});
            skPoint(sketch, "E382", {"position": v(-36.7, 2.33) * mm});
            skLineSegment(sketch, "E383.0", {"start": v(121, 39.06) * mm, "end": v(121.6, 33.48) * mm, "construction": true});
            skLineSegment(sketch, "E383.1", {"start": v(121.6, 33.48) * mm, "end": v(120.47, 27.98) * mm, "construction": true});
            skLineSegment(sketch, "E383.2", {"start": v(120.47, 27.98) * mm, "end": v(117.68, 23.1) * mm, "construction": true});
            skLineSegment(sketch, "E383.3", {"start": v(117.68, 23.1) * mm, "end": v(113.52, 19.33) * mm, "construction": true});
            skLineSegment(sketch, "E383.4", {"start": v(113.52, 19.33) * mm, "end": v(108.4, 17.02) * mm, "construction": true});
            skLineSegment(sketch, "E383.5", {"start": v(108.4, 17.02) * mm, "end": v(102.82, 16.41) * mm, "construction": true});
            skLineSegment(sketch, "E383.6", {"start": v(102.82, 16.41) * mm, "end": v(97.32, 17.55) * mm, "construction": true});
            skLineSegment(sketch, "E383.7", {"start": v(97.32, 17.55) * mm, "end": v(92.45, 20.34) * mm, "construction": true});
            skLineSegment(sketch, "E383.8", {"start": v(92.45, 20.34) * mm, "end": v(88.67, 24.5) * mm, "construction": true});
            skLineSegment(sketch, "E383.9", {"start": v(88.67, 24.5) * mm, "end": v(86.36, 29.62) * mm, "construction": true});
            skLineSegment(sketch, "E383.10", {"start": v(86.36, 29.62) * mm, "end": v(85.75, 35.2) * mm, "construction": true});
            skLineSegment(sketch, "E383.11", {"start": v(85.75, 35.2) * mm, "end": v(86.9, 40.7) * mm, "construction": true});
            skLineSegment(sketch, "E383.12", {"start": v(86.9, 40.7) * mm, "end": v(89.68, 45.58) * mm, "construction": true});
            skLineSegment(sketch, "E383.13", {"start": v(89.68, 45.58) * mm, "end": v(93.84, 49.35) * mm, "construction": true});
            skLineSegment(sketch, "E383.14", {"start": v(93.84, 49.35) * mm, "end": v(98.96, 51.66) * mm, "construction": true});
            skLineSegment(sketch, "E383.15", {"start": v(98.96, 51.66) * mm, "end": v(104.54, 52.27) * mm, "construction": true});
            skLineSegment(sketch, "E383.16", {"start": v(104.54, 52.27) * mm, "end": v(110.04, 51.13) * mm, "construction": true});
            skLineSegment(sketch, "E383.17", {"start": v(110.04, 51.13) * mm, "end": v(114.91, 48.34) * mm, "construction": true});
            skLineSegment(sketch, "E383.18", {"start": v(114.91, 48.34) * mm, "end": v(118.7, 44.18) * mm, "construction": true});
            skLineSegment(sketch, "E383.19", {"start": v(118.7, 44.18) * mm, "end": v(121, 39.06) * mm, "construction": true});
            skLineSegment(sketch, "E384", {"start": v(115.66, 55.6) * mm, "end": v(115.9, 55.45) * mm});
            skLineSegment(sketch, "E385", {"start": v(116.37, 53.88) * mm, "end": v(115.4, 50.2) * mm});
            skLineSegment(sketch, "E386", {"start": v(113.25, 49.3) * mm, "end": v(111.7, 50.18) * mm});
            skLineSegment(sketch, "E387", {"start": v(111.39, 52.5) * mm, "end": v(114.07, 55.2) * mm});
            skArc(sketch, "E388.filletArc", {"start": v(115.9, 55.45) * mm, "mid": v(114.95, 55.64) * mm, "end": v(114.07, 55.2) * mm});
            skArc(sketch, "E389.filletArc", {"start": v(116.37, 53.88) * mm, "mid": v(116.3, 54.86) * mm, "end": v(115.66, 55.6) * mm});
            skArc(sketch, "E390.filletArc", {"start": v(113.25, 49.3) * mm, "mid": v(114.55, 49.21) * mm, "end": v(115.4, 50.2) * mm});
            skArc(sketch, "E391.filletArc", {"start": v(111.39, 52.5) * mm, "mid": v(110.97, 51.26) * mm, "end": v(111.7, 50.18) * mm});
            skPoint(sketch, "E392", {"position": v(112.48, 49.73) * mm});
            skLineSegment(sketch, "E393", {"start": v(121.64, 50.85) * mm, "end": v(121.83, 50.64) * mm});
            skLineSegment(sketch, "E394", {"start": v(121.8, 49) * mm, "end": v(119.73, 45.8) * mm});
            skLineSegment(sketch, "E395", {"start": v(117.4, 45.6) * mm, "end": v(116.2, 46.92) * mm});
            skLineSegment(sketch, "E396", {"start": v(116.62, 49.22) * mm, "end": v(120, 50.97) * mm});
            skArc(sketch, "E397.filletArc", {"start": v(121.83, 50.64) * mm, "mid": v(120.98, 51.11) * mm, "end": v(120, 50.97) * mm});
            skArc(sketch, "E398.filletArc", {"start": v(121.8, 49) * mm, "mid": v(122.03, 49.95) * mm, "end": v(121.64, 50.85) * mm});
            skArc(sketch, "E399.filletArc", {"start": v(117.4, 45.6) * mm, "mid": v(118.61, 45.13) * mm, "end": v(119.73, 45.8) * mm});
            skArc(sketch, "E400.filletArc", {"start": v(116.62, 49.22) * mm, "mid": v(115.84, 48.17) * mm, "end": v(116.2, 46.92) * mm});
            skPoint(sketch, "E401", {"position": v(116.8, 46.26) * mm});
            skLineSegment(sketch, "E402", {"start": v(125.86, 44.5) * mm, "end": v(125.98, 44.23) * mm});
            skLineSegment(sketch, "E403", {"start": v(125.44, 42.69) * mm, "end": v(122.49, 40.28) * mm});
            skLineSegment(sketch, "E404", {"start": v(120.2, 40.81) * mm, "end": v(119.48, 42.44) * mm});
            skLineSegment(sketch, "E405", {"start": v(120.59, 44.5) * mm, "end": v(124.35, 45.1) * mm});
            skArc(sketch, "E406.filletArc", {"start": v(125.98, 44.23) * mm, "mid": v(125.31, 44.95) * mm, "end": v(124.35, 45.1) * mm});
            skArc(sketch, "E407.filletArc", {"start": v(125.44, 42.69) * mm, "mid": v(125.96, 43.52) * mm, "end": v(125.86, 44.5) * mm});
            skArc(sketch, "E408.filletArc", {"start": v(120.2, 40.81) * mm, "mid": v(121.22, 39.98) * mm, "end": v(122.49, 40.28) * mm});
            skArc(sketch, "E409.filletArc", {"start": v(120.59, 44.5) * mm, "mid": v(119.52, 43.74) * mm, "end": v(119.48, 42.44) * mm});
            skPoint(sketch, "E410", {"position": v(119.84, 41.62) * mm});
            skLineSegment(sketch, "E411", {"start": v(93.53, 56.52) * mm, "end": v(93.8, 56.64) * mm});
            skLineSegment(sketch, "E412", {"start": v(95.33, 56.1) * mm, "end": v(97.74, 53.15) * mm});
            skLineSegment(sketch, "E413", {"start": v(97.2, 50.87) * mm, "end": v(95.59, 50.14) * mm});
            skLineSegment(sketch, "E414", {"start": v(93.53, 51.25) * mm, "end": v(92.91, 55) * mm});
            skArc(sketch, "E415.filletArc", {"start": v(93.8, 56.64) * mm, "mid": v(93.07, 55.97) * mm, "end": v(92.91, 55) * mm});
            skArc(sketch, "E416.filletArc", {"start": v(95.33, 56.1) * mm, "mid": v(94.5, 56.62) * mm, "end": v(93.53, 56.52) * mm});
            skArc(sketch, "E417.filletArc", {"start": v(97.2, 50.87) * mm, "mid": v(98.04, 51.88) * mm, "end": v(97.74, 53.15) * mm});
            skArc(sketch, "E418.filletArc", {"start": v(93.53, 51.25) * mm, "mid": v(94.28, 50.19) * mm, "end": v(95.59, 50.14) * mm});
            skPoint(sketch, "E419", {"position": v(96.4, 50.5) * mm});
            skLineSegment(sketch, "E420", {"start": v(100.88, 58.58) * mm, "end": v(101.17, 58.6) * mm});
            skLineSegment(sketch, "E421", {"start": v(102.46, 57.61) * mm, "end": v(103.85, 54.06) * mm});
            skLineSegment(sketch, "E422", {"start": v(102.63, 52.06) * mm, "end": v(100.86, 51.87) * mm});
            skLineSegment(sketch, "E423", {"start": v(99.25, 53.56) * mm, "end": v(99.83, 57.32) * mm});
            skArc(sketch, "E424.filletArc", {"start": v(101.17, 58.6) * mm, "mid": v(100.28, 58.2) * mm, "end": v(99.83, 57.32) * mm});
            skArc(sketch, "E425.filletArc", {"start": v(102.46, 57.61) * mm, "mid": v(101.83, 58.36) * mm, "end": v(100.88, 58.58) * mm});
            skArc(sketch, "E426.filletArc", {"start": v(102.63, 52.06) * mm, "mid": v(103.73, 52.76) * mm, "end": v(103.85, 54.06) * mm});
            skArc(sketch, "E427.filletArc", {"start": v(99.25, 53.56) * mm, "mid": v(99.64, 52.31) * mm, "end": v(100.86, 51.87) * mm});
            skPoint(sketch, "E428", {"position": v(101.75, 51.96) * mm});
            skLineSegment(sketch, "E429", {"start": v(127.91, 37.14) * mm, "end": v(127.95, 36.86) * mm});
            skLineSegment(sketch, "E430", {"start": v(126.95, 35.56) * mm, "end": v(123.4, 34.18) * mm});
            skLineSegment(sketch, "E431", {"start": v(121.4, 35.39) * mm, "end": v(121.2, 37.16) * mm});
            skLineSegment(sketch, "E432", {"start": v(122.9, 38.78) * mm, "end": v(126.66, 38.2) * mm});
            skArc(sketch, "E433.filletArc", {"start": v(127.95, 36.86) * mm, "mid": v(127.53, 37.74) * mm, "end": v(126.66, 38.2) * mm});
            skArc(sketch, "E434.filletArc", {"start": v(126.95, 35.56) * mm, "mid": v(127.7, 36.19) * mm, "end": v(127.91, 37.14) * mm});
            skArc(sketch, "E435.filletArc", {"start": v(121.4, 35.39) * mm, "mid": v(122.1, 34.29) * mm, "end": v(123.4, 34.18) * mm});
            skArc(sketch, "E436.filletArc", {"start": v(122.9, 38.78) * mm, "mid": v(121.65, 38.38) * mm, "end": v(121.2, 37.16) * mm});
            skPoint(sketch, "E437", {"position": v(121.3, 36.27) * mm});
            skLineSegment(sketch, "E438", {"start": v(127.6, 29.52) * mm, "end": v(127.53, 29.23) * mm});
            skLineSegment(sketch, "E439", {"start": v(126.19, 28.3) * mm, "end": v(122.38, 28.1) * mm});
            skLineSegment(sketch, "E440", {"start": v(120.86, 29.86) * mm, "end": v(121.22, 31.6) * mm});
            skLineSegment(sketch, "E441", {"start": v(123.33, 32.62) * mm, "end": v(126.73, 30.9) * mm});
            skArc(sketch, "E442.filletArc", {"start": v(127.53, 29.23) * mm, "mid": v(127.42, 30.2) * mm, "end": v(126.73, 30.9) * mm});
            skArc(sketch, "E443.filletArc", {"start": v(126.19, 28.3) * mm, "mid": v(127.1, 28.67) * mm, "end": v(127.6, 29.52) * mm});
            skArc(sketch, "E444.filletArc", {"start": v(120.86, 29.86) * mm, "mid": v(121.18, 28.6) * mm, "end": v(122.38, 28.1) * mm});
            skArc(sketch, "E445.filletArc", {"start": v(123.33, 32.62) * mm, "mid": v(122.02, 32.63) * mm, "end": v(121.22, 31.6) * mm});
            skPoint(sketch, "E446", {"position": v(121.04, 30.73) * mm});
            skLineSegment(sketch, "E447", {"start": v(108.72, 58.21) * mm, "end": v(109, 58.14) * mm});
            skLineSegment(sketch, "E448", {"start": v(109.88, 56.77) * mm, "end": v(109.97, 52.96) * mm});
            skLineSegment(sketch, "E449", {"start": v(108.15, 51.49) * mm, "end": v(106.42, 51.9) * mm});
            skLineSegment(sketch, "E450", {"start": v(105.48, 54.05) * mm, "end": v(107.3, 57.4) * mm});
            skArc(sketch, "E451.filletArc", {"start": v(109, 58.14) * mm, "mid": v(108.03, 58.06) * mm, "end": v(107.3, 57.4) * mm});
            skArc(sketch, "E452.filletArc", {"start": v(109.88, 56.77) * mm, "mid": v(109.55, 57.69) * mm, "end": v(108.72, 58.21) * mm});
            skArc(sketch, "E453.filletArc", {"start": v(108.15, 51.49) * mm, "mid": v(109.43, 51.77) * mm, "end": v(109.97, 52.96) * mm});
            skArc(sketch, "E454.filletArc", {"start": v(105.48, 54.05) * mm, "mid": v(105.42, 52.75) * mm, "end": v(106.42, 51.9) * mm});
            skPoint(sketch, "E455", {"position": v(107.29, 51.7) * mm});
            skLineSegment(sketch, "E456", {"start": v(87.17, 52.3) * mm, "end": v(87.38, 52.5) * mm});
            skLineSegment(sketch, "E457", {"start": v(89.02, 52.45) * mm, "end": v(92.22, 50.4) * mm});
            skLineSegment(sketch, "E458", {"start": v(92.42, 48.06) * mm, "end": v(91.1, 46.87) * mm});
            skLineSegment(sketch, "E459", {"start": v(88.8, 47.28) * mm, "end": v(87.05, 50.67) * mm});
            skArc(sketch, "E460.filletArc", {"start": v(87.38, 52.5) * mm, "mid": v(86.9, 51.64) * mm, "end": v(87.05, 50.67) * mm});
            skArc(sketch, "E461.filletArc", {"start": v(89.02, 52.45) * mm, "mid": v(88.07, 52.7) * mm, "end": v(87.17, 52.3) * mm});
            skArc(sketch, "E462.filletArc", {"start": v(92.42, 48.06) * mm, "mid": v(92.9, 49.27) * mm, "end": v(92.22, 50.4) * mm});
            skArc(sketch, "E463.filletArc", {"start": v(88.8, 47.28) * mm, "mid": v(89.85, 46.5) * mm, "end": v(91.1, 46.87) * mm});
            skPoint(sketch, "E464", {"position": v(91.76, 47.46) * mm});
            skLineSegment(sketch, "E465", {"start": v(82.43, 46.32) * mm, "end": v(82.57, 46.57) * mm});
            skLineSegment(sketch, "E466", {"start": v(84.14, 47.04) * mm, "end": v(87.82, 46.07) * mm});
            skLineSegment(sketch, "E467", {"start": v(88.73, 43.9) * mm, "end": v(87.85, 42.37) * mm});
            skLineSegment(sketch, "E468", {"start": v(85.53, 42.05) * mm, "end": v(82.82, 44.73) * mm});
            skArc(sketch, "E469.filletArc", {"start": v(82.57, 46.57) * mm, "mid": v(82.38, 45.6) * mm, "end": v(82.82, 44.73) * mm});
            skArc(sketch, "E470.filletArc", {"start": v(84.14, 47.04) * mm, "mid": v(83.16, 46.97) * mm, "end": v(82.43, 46.32) * mm});
            skArc(sketch, "E471.filletArc", {"start": v(88.73, 43.9) * mm, "mid": v(88.8, 45.21) * mm, "end": v(87.82, 46.07) * mm});
            skArc(sketch, "E472.filletArc", {"start": v(85.53, 42.05) * mm, "mid": v(86.76, 41.64) * mm, "end": v(87.85, 42.37) * mm});
            skPoint(sketch, "E473", {"position": v(88.29, 43.14) * mm});
            skLineSegment(sketch, "E474", {"start": v(79.77, 39.16) * mm, "end": v(79.83, 39.45) * mm});
            skLineSegment(sketch, "E475", {"start": v(81.17, 40.38) * mm, "end": v(84.98, 40.6) * mm});
            skLineSegment(sketch, "E476", {"start": v(86.5, 38.82) * mm, "end": v(86.14, 37.08) * mm});
            skLineSegment(sketch, "E477", {"start": v(84.03, 36.06) * mm, "end": v(80.63, 37.78) * mm});
            skArc(sketch, "E478.filletArc", {"start": v(79.83, 39.45) * mm, "mid": v(79.94, 38.48) * mm, "end": v(80.63, 37.78) * mm});
            skArc(sketch, "E479.filletArc", {"start": v(81.17, 40.38) * mm, "mid": v(80.26, 40) * mm, "end": v(79.77, 39.16) * mm});
            skArc(sketch, "E480.filletArc", {"start": v(86.5, 38.82) * mm, "mid": v(86.18, 40.08) * mm, "end": v(84.98, 40.6) * mm});
            skArc(sketch, "E481.filletArc", {"start": v(84.03, 36.06) * mm, "mid": v(85.34, 36.05) * mm, "end": v(86.14, 37.08) * mm});
            skPoint(sketch, "E482", {"position": v(86.32, 37.95) * mm});
            skLineSegment(sketch, "E483", {"start": v(79.45, 31.54) * mm, "end": v(79.41, 31.83) * mm});
            skLineSegment(sketch, "E484", {"start": v(80.4, 33.13) * mm, "end": v(83.96, 34.5) * mm});
            skLineSegment(sketch, "E485", {"start": v(85.96, 33.3) * mm, "end": v(86.15, 31.53) * mm});
            skLineSegment(sketch, "E486", {"start": v(84.46, 29.9) * mm, "end": v(80.7, 30.49) * mm});
            skArc(sketch, "E487.filletArc", {"start": v(79.41, 31.83) * mm, "mid": v(79.83, 30.94) * mm, "end": v(80.7, 30.49) * mm});
            skArc(sketch, "E488.filletArc", {"start": v(80.4, 33.13) * mm, "mid": v(79.66, 32.5) * mm, "end": v(79.45, 31.54) * mm});
            skArc(sketch, "E489.filletArc", {"start": v(85.96, 33.3) * mm, "mid": v(85.26, 34.4) * mm, "end": v(83.96, 34.5) * mm});
            skArc(sketch, "E490.filletArc", {"start": v(84.46, 29.9) * mm, "mid": v(85.7, 30.3) * mm, "end": v(86.15, 31.53) * mm});
            skPoint(sketch, "E491", {"position": v(86.06, 32.4) * mm});
            skLineSegment(sketch, "E492", {"start": v(81.5, 24.19) * mm, "end": v(81.38, 24.45) * mm});
            skLineSegment(sketch, "E493", {"start": v(81.92, 26) * mm, "end": v(84.87, 28.4) * mm});
            skLineSegment(sketch, "E494", {"start": v(87.15, 27.87) * mm, "end": v(87.88, 26.25) * mm});
            skLineSegment(sketch, "E495", {"start": v(86.77, 24.19) * mm, "end": v(83.01, 23.57) * mm});
            skArc(sketch, "E496.filletArc", {"start": v(81.38, 24.45) * mm, "mid": v(82.05, 23.74) * mm, "end": v(83.01, 23.57) * mm});
            skArc(sketch, "E497.filletArc", {"start": v(81.92, 26) * mm, "mid": v(81.4, 25.16) * mm, "end": v(81.5, 24.19) * mm});
            skArc(sketch, "E498.filletArc", {"start": v(87.15, 27.87) * mm, "mid": v(86.14, 28.7) * mm, "end": v(84.87, 28.4) * mm});
            skArc(sketch, "E499.filletArc", {"start": v(86.77, 24.19) * mm, "mid": v(87.84, 24.94) * mm, "end": v(87.88, 26.25) * mm});
            skPoint(sketch, "E500", {"position": v(87.52, 27.06) * mm});
            skLineSegment(sketch, "E501", {"start": v(113.83, 12.16) * mm, "end": v(113.57, 12.04) * mm});
            skLineSegment(sketch, "E502", {"start": v(112.03, 12.58) * mm, "end": v(109.62, 15.53) * mm});
            skLineSegment(sketch, "E503", {"start": v(110.15, 17.81) * mm, "end": v(111.77, 18.54) * mm});
            skLineSegment(sketch, "E504", {"start": v(113.84, 17.44) * mm, "end": v(114.45, 13.68) * mm});
            skArc(sketch, "E505.filletArc", {"start": v(113.57, 12.04) * mm, "mid": v(114.29, 12.7) * mm, "end": v(114.45, 13.68) * mm});
            skArc(sketch, "E506.filletArc", {"start": v(112.03, 12.58) * mm, "mid": v(112.86, 12.07) * mm, "end": v(113.83, 12.16) * mm});
            skArc(sketch, "E507.filletArc", {"start": v(110.15, 17.81) * mm, "mid": v(109.32, 16.8) * mm, "end": v(109.62, 15.53) * mm});
            skArc(sketch, "E508.filletArc", {"start": v(113.84, 17.44) * mm, "mid": v(113.08, 18.5) * mm, "end": v(111.77, 18.54) * mm});
            skPoint(sketch, "E509", {"position": v(110.96, 18.18) * mm});
            skLineSegment(sketch, "E510", {"start": v(106.48, 10.1) * mm, "end": v(106.2, 10.08) * mm});
            skLineSegment(sketch, "E511", {"start": v(104.9, 11.07) * mm, "end": v(103.52, 14.62) * mm});
            skLineSegment(sketch, "E512", {"start": v(104.73, 16.62) * mm, "end": v(106.5, 16.81) * mm});
            skLineSegment(sketch, "E513", {"start": v(108.11, 15.12) * mm, "end": v(107.53, 11.36) * mm});
            skArc(sketch, "E514.filletArc", {"start": v(106.2, 10.08) * mm, "mid": v(107.08, 10.49) * mm, "end": v(107.53, 11.36) * mm});
            skArc(sketch, "E515.filletArc", {"start": v(104.9, 11.07) * mm, "mid": v(105.53, 10.32) * mm, "end": v(106.48, 10.1) * mm});
            skArc(sketch, "E516.filletArc", {"start": v(104.73, 16.62) * mm, "mid": v(103.63, 15.92) * mm, "end": v(103.52, 14.62) * mm});
            skArc(sketch, "E517.filletArc", {"start": v(108.11, 15.12) * mm, "mid": v(107.72, 16.37) * mm, "end": v(106.5, 16.81) * mm});
            skPoint(sketch, "E518", {"position": v(105.61, 16.72) * mm});
            skLineSegment(sketch, "E519", {"start": v(120.2, 16.38) * mm, "end": v(119.98, 16.19) * mm});
            skLineSegment(sketch, "E520", {"start": v(118.34, 16.23) * mm, "end": v(115.14, 18.29) * mm});
            skLineSegment(sketch, "E521", {"start": v(114.94, 20.62) * mm, "end": v(116.26, 21.82) * mm});
            skLineSegment(sketch, "E522", {"start": v(118.56, 21.4) * mm, "end": v(120.3, 18.01) * mm});
            skArc(sketch, "E523.filletArc", {"start": v(119.98, 16.19) * mm, "mid": v(120.45, 17.04) * mm, "end": v(120.3, 18.01) * mm});
            skArc(sketch, "E524.filletArc", {"start": v(118.34, 16.23) * mm, "mid": v(119.3, 16) * mm, "end": v(120.2, 16.38) * mm});
            skArc(sketch, "E525.filletArc", {"start": v(114.94, 20.62) * mm, "mid": v(114.47, 19.4) * mm, "end": v(115.14, 18.29) * mm});
            skArc(sketch, "E526.filletArc", {"start": v(118.56, 21.4) * mm, "mid": v(117.51, 22.18) * mm, "end": v(116.26, 21.82) * mm});
            skPoint(sketch, "E527", {"position": v(115.6, 21.22) * mm});
            skLineSegment(sketch, "E528", {"start": v(85.72, 17.83) * mm, "end": v(85.53, 18.04) * mm});
            skLineSegment(sketch, "E529", {"start": v(85.57, 19.68) * mm, "end": v(87.63, 22.88) * mm});
            skLineSegment(sketch, "E530", {"start": v(89.96, 23.08) * mm, "end": v(91.16, 21.76) * mm});
            skLineSegment(sketch, "E531", {"start": v(90.74, 19.46) * mm, "end": v(87.35, 17.71) * mm});
            skArc(sketch, "E532.filletArc", {"start": v(85.53, 18.04) * mm, "mid": v(86.38, 17.57) * mm, "end": v(87.35, 17.71) * mm});
            skArc(sketch, "E533.filletArc", {"start": v(85.57, 19.68) * mm, "mid": v(85.33, 18.73) * mm, "end": v(85.72, 17.83) * mm});
            skArc(sketch, "E534.filletArc", {"start": v(89.96, 23.08) * mm, "mid": v(88.75, 23.56) * mm, "end": v(87.63, 22.88) * mm});
            skArc(sketch, "E535.filletArc", {"start": v(90.74, 19.46) * mm, "mid": v(91.52, 20.5) * mm, "end": v(91.16, 21.76) * mm});
            skPoint(sketch, "E536", {"position": v(90.56, 22.42) * mm});
            skLineSegment(sketch, "E537", {"start": v(124.93, 22.36) * mm, "end": v(124.79, 22.11) * mm});
            skLineSegment(sketch, "E538", {"start": v(123.22, 21.65) * mm, "end": v(119.54, 22.62) * mm});
            skLineSegment(sketch, "E539", {"start": v(118.63, 24.77) * mm, "end": v(119.51, 26.32) * mm});
            skLineSegment(sketch, "E540", {"start": v(121.83, 26.63) * mm, "end": v(124.54, 23.95) * mm});
            skArc(sketch, "E541.filletArc", {"start": v(124.79, 22.11) * mm, "mid": v(124.98, 23.07) * mm, "end": v(124.54, 23.95) * mm});
            skArc(sketch, "E542.filletArc", {"start": v(123.22, 21.65) * mm, "mid": v(124.2, 21.72) * mm, "end": v(124.93, 22.36) * mm});
            skArc(sketch, "E543.filletArc", {"start": v(118.63, 24.77) * mm, "mid": v(118.55, 23.47) * mm, "end": v(119.54, 22.62) * mm});
            skArc(sketch, "E544.filletArc", {"start": v(121.83, 26.63) * mm, "mid": v(120.6, 27.05) * mm, "end": v(119.51, 26.32) * mm});
            skPoint(sketch, "E545", {"position": v(119.07, 25.55) * mm});
            skLineSegment(sketch, "E546", {"start": v(98.86, 10.43) * mm, "end": v(98.57, 10.49) * mm});
            skLineSegment(sketch, "E547", {"start": v(97.65, 11.83) * mm, "end": v(97.43, 15.64) * mm});
            skLineSegment(sketch, "E548", {"start": v(99.2, 17.16) * mm, "end": v(100.94, 16.8) * mm});
            skLineSegment(sketch, "E549", {"start": v(101.96, 14.7) * mm, "end": v(100.24, 11.3) * mm});
            skArc(sketch, "E550.filletArc", {"start": v(98.57, 10.49) * mm, "mid": v(99.55, 10.6) * mm, "end": v(100.24, 11.3) * mm});
            skArc(sketch, "E551.filletArc", {"start": v(97.65, 11.83) * mm, "mid": v(98.01, 10.92) * mm, "end": v(98.86, 10.43) * mm});
            skArc(sketch, "E552.filletArc", {"start": v(99.2, 17.16) * mm, "mid": v(97.94, 16.84) * mm, "end": v(97.43, 15.64) * mm});
            skArc(sketch, "E553.filletArc", {"start": v(101.96, 14.7) * mm, "mid": v(101.97, 16) * mm, "end": v(100.94, 16.8) * mm});
            skPoint(sketch, "E554", {"position": v(100.07, 16.98) * mm});
            skLineSegment(sketch, "E555", {"start": v(91.7, 13.09) * mm, "end": v(91.45, 13.23) * mm});
            skLineSegment(sketch, "E556", {"start": v(90.99, 14.8) * mm, "end": v(91.96, 18.48) * mm});
            skLineSegment(sketch, "E557", {"start": v(94.11, 19.39) * mm, "end": v(95.66, 18.5) * mm});
            skLineSegment(sketch, "E558", {"start": v(95.97, 16.19) * mm, "end": v(93.29, 13.48) * mm});
            skArc(sketch, "E559.filletArc", {"start": v(91.45, 13.23) * mm, "mid": v(92.41, 13.05) * mm, "end": v(93.29, 13.48) * mm});
            skArc(sketch, "E560.filletArc", {"start": v(90.99, 14.8) * mm, "mid": v(91.05, 13.82) * mm, "end": v(91.7, 13.09) * mm});
            skArc(sketch, "E561.filletArc", {"start": v(94.11, 19.39) * mm, "mid": v(92.81, 19.47) * mm, "end": v(91.96, 18.48) * mm});
            skArc(sketch, "E562.filletArc", {"start": v(95.97, 16.19) * mm, "mid": v(96.39, 17.43) * mm, "end": v(95.66, 18.5) * mm});
            skPoint(sketch, "E563", {"position": v(94.88, 18.95) * mm});
            skSolve(sketch);
        }
        {
            var Q0;
            {var subQ1=sQuery(id+"F0.wireOp",EDGE,"E385");Q0=makeQuery(id+"F0.imprint","IMPRINT",FACE,{"disambiguationData":[TD([[makeQuery(id+"F0.imprint","IMPRINT",EDGE,{"derivedFrom":subQ1}),-1.0]])]});}
            var Q1;
            {var subQ4=sQuery(id+"F0.wireOp",EDGE,"E484");Q1=makeQuery(id+"F0.imprint","IMPRINT",FACE,{"disambiguationData":[TD([[makeQuery(id+"F0.imprint","IMPRINT",EDGE,{"derivedFrom":subQ4}),-1.0]])]});}
            var Q2;
            {var subQ4=sQuery(id+"F0.wireOp",EDGE,"E448");Q2=makeQuery(id+"F0.imprint","IMPRINT",FACE,{"disambiguationData":[TD([[makeQuery(id+"F0.imprint","IMPRINT",EDGE,{"derivedFrom":subQ4}),-1.0]])]});}
            var Q3;
            {var subQ9=sQuery(id+"F0.wireOp",EDGE,"E511");Q3=makeQuery(id+"F0.imprint","IMPRINT",FACE,{"disambiguationData":[TD([[makeQuery(id+"F0.imprint","IMPRINT",EDGE,{"derivedFrom":subQ9}),-1.0]])]});}
            var Q4;
            {var subQ9=sQuery(id+"F0.wireOp",EDGE,"E556");Q4=makeQuery(id+"F0.imprint","IMPRINT",FACE,{"disambiguationData":[TD([[makeQuery(id+"F0.imprint","IMPRINT",EDGE,{"derivedFrom":subQ9}),-1.0]])]});}
            var Q5;
            {var subQ9=sQuery(id+"F0.wireOp",EDGE,"E466");Q5=makeQuery(id+"F0.imprint","IMPRINT",FACE,{"disambiguationData":[TD([[makeQuery(id+"F0.imprint","IMPRINT",EDGE,{"derivedFrom":subQ9}),-1.0]])]});}
            var Q6;
            {var subQ1=sQuery(id+"F0.wireOp",EDGE,"E502");Q6=makeQuery(id+"F0.imprint","IMPRINT",FACE,{"disambiguationData":[TD([[makeQuery(id+"F0.imprint","IMPRINT",EDGE,{"derivedFrom":subQ1}),-1.0]])]});}
            var Q7;
            {var subQ4=sQuery(id+"F0.wireOp",EDGE,"E493");Q7=makeQuery(id+"F0.imprint","IMPRINT",FACE,{"disambiguationData":[TD([[makeQuery(id+"F0.imprint","IMPRINT",EDGE,{"derivedFrom":subQ4}),-1.0]])]});}
            var Q8;
            {var subQ4=sQuery(id+"F0.wireOp",EDGE,"E394");Q8=makeQuery(id+"F0.imprint","IMPRINT",FACE,{"disambiguationData":[TD([[makeQuery(id+"F0.imprint","IMPRINT",EDGE,{"derivedFrom":subQ4}),-1.0]])]});}
            var Q9;
            {var subQ1=sQuery(id+"F0.wireOp",EDGE,"E439");Q9=makeQuery(id+"F0.imprint","IMPRINT",FACE,{"disambiguationData":[TD([[makeQuery(id+"F0.imprint","IMPRINT",EDGE,{"derivedFrom":subQ1}),-1.0]])]});}
            var Q10;
            {var subQ4=sQuery(id+"F0.wireOp",EDGE,"E430");Q10=makeQuery(id+"F0.imprint","IMPRINT",FACE,{"disambiguationData":[TD([[makeQuery(id+"F0.imprint","IMPRINT",EDGE,{"derivedFrom":subQ4}),-1.0]])]});}
            var Q11;
            {var subQ4=sQuery(id+"F0.wireOp",EDGE,"E475");Q11=makeQuery(id+"F0.imprint","IMPRINT",FACE,{"disambiguationData":[TD([[makeQuery(id+"F0.imprint","IMPRINT",EDGE,{"derivedFrom":subQ4}),-1.0]])]});}
            var Q12;
            {var subQ4=sQuery(id+"F0.wireOp",EDGE,"E403");Q12=makeQuery(id+"F0.imprint","IMPRINT",FACE,{"disambiguationData":[TD([[makeQuery(id+"F0.imprint","IMPRINT",EDGE,{"derivedFrom":subQ4}),-1.0]])]});}
            var Q13;
            {var subQ4=sQuery(id+"F0.wireOp",EDGE,"E421");Q13=makeQuery(id+"F0.imprint","IMPRINT",FACE,{"disambiguationData":[TD([[makeQuery(id+"F0.imprint","IMPRINT",EDGE,{"derivedFrom":subQ4}),-1.0]])]});}
            var Q14;
            {var subQ4=sQuery(id+"F0.wireOp",EDGE,"E520");Q14=makeQuery(id+"F0.imprint","IMPRINT",FACE,{"disambiguationData":[TD([[makeQuery(id+"F0.imprint","IMPRINT",EDGE,{"derivedFrom":subQ4}),-1.0]])]});}
            var Q15;
            {var subQ4=sQuery(id+"F0.wireOp",EDGE,"E457");Q15=makeQuery(id+"F0.imprint","IMPRINT",FACE,{"disambiguationData":[TD([[makeQuery(id+"F0.imprint","IMPRINT",EDGE,{"derivedFrom":subQ4}),-1.0]])]});}
            var Q16;
            {var subQ4=sQuery(id+"F0.wireOp",EDGE,"E538");Q16=makeQuery(id+"F0.imprint","IMPRINT",FACE,{"disambiguationData":[TD([[makeQuery(id+"F0.imprint","IMPRINT",EDGE,{"derivedFrom":subQ4}),-1.0]])]});}
            var Q17;
            {var subQ1=sQuery(id+"F0.wireOp",EDGE,"E412");Q17=makeQuery(id+"F0.imprint","IMPRINT",FACE,{"disambiguationData":[TD([[makeQuery(id+"F0.imprint","IMPRINT",EDGE,{"derivedFrom":subQ1}),-1.0]])]});}
            var Q18;
            {var subQ4=sQuery(id+"F0.wireOp",EDGE,"E547");Q18=makeQuery(id+"F0.imprint","IMPRINT",FACE,{"disambiguationData":[TD([[makeQuery(id+"F0.imprint","IMPRINT",EDGE,{"derivedFrom":subQ4}),-1.0]])]});}
            var Q19;
            {var subQ4=sQuery(id+"F0.wireOp",EDGE,"E529");Q19=makeQuery(id+"F0.imprint","IMPRINT",FACE,{"disambiguationData":[TD([[makeQuery(id+"F0.imprint","IMPRINT",EDGE,{"derivedFrom":subQ4}),-1.0]])]});}
            var Q20;
            Q20=makeQuery(id+"F0.imprint","IMPRINT",FACE,{"disambiguationData":[TD([[makeQuery(id+"F0.imprint","IMPRINT",EDGE,{"derivedFrom":sQuery(id+"F0.wireOp",EDGE,"E3")}),-1.0]])]});
            var Q21;
            {var subQ5=sQuery(id+"F0.wireOp",EDGE,"E503");Q21=makeQuery(id+"F0.imprint","IMPRINT",FACE,{"disambiguationData":[TD([[makeQuery(id+"F0.imprint","IMPRINT",EDGE,{"derivedFrom":subQ5}),-1.0]])]});}
            var Q22;
            {var subQ5=sQuery(id+"F0.wireOp",EDGE,"E494");Q22=makeQuery(id+"F0.imprint","IMPRINT",FACE,{"disambiguationData":[TD([[makeQuery(id+"F0.imprint","IMPRINT",EDGE,{"derivedFrom":subQ5}),-1.0]])]});}
            var Q23;
            {var subQ5=sQuery(id+"F0.wireOp",EDGE,"E449");Q23=makeQuery(id+"F0.imprint","IMPRINT",FACE,{"disambiguationData":[TD([[makeQuery(id+"F0.imprint","IMPRINT",EDGE,{"derivedFrom":subQ5}),-1.0]])]});}
            var Q24;
            {var subQ5=sQuery(id+"F0.wireOp",EDGE,"E539");Q24=makeQuery(id+"F0.imprint","IMPRINT",FACE,{"disambiguationData":[TD([[makeQuery(id+"F0.imprint","IMPRINT",EDGE,{"derivedFrom":subQ5}),-1.0]])]});}
            var Q25;
            {var subQ5=sQuery(id+"F0.wireOp",EDGE,"E548");Q25=makeQuery(id+"F0.imprint","IMPRINT",FACE,{"disambiguationData":[TD([[makeQuery(id+"F0.imprint","IMPRINT",EDGE,{"derivedFrom":subQ5}),-1.0]])]});}
            var Q26;
            {var subQ5=sQuery(id+"F0.wireOp",EDGE,"E431");Q26=makeQuery(id+"F0.imprint","IMPRINT",FACE,{"disambiguationData":[TD([[makeQuery(id+"F0.imprint","IMPRINT",EDGE,{"derivedFrom":subQ5}),-1.0]])]});}
            var Q27;
            {var subQ5=sQuery(id+"F0.wireOp",EDGE,"E386");Q27=makeQuery(id+"F0.imprint","IMPRINT",FACE,{"disambiguationData":[TD([[makeQuery(id+"F0.imprint","IMPRINT",EDGE,{"derivedFrom":subQ5}),-1.0]])]});}
            var Q28;
            {var subQ5=sQuery(id+"F0.wireOp",EDGE,"E557");Q28=makeQuery(id+"F0.imprint","IMPRINT",FACE,{"disambiguationData":[TD([[makeQuery(id+"F0.imprint","IMPRINT",EDGE,{"derivedFrom":subQ5}),-1.0]])]});}
            var Q29;
            {var subQ5=sQuery(id+"F0.wireOp",EDGE,"E404");Q29=makeQuery(id+"F0.imprint","IMPRINT",FACE,{"disambiguationData":[TD([[makeQuery(id+"F0.imprint","IMPRINT",EDGE,{"derivedFrom":subQ5}),-1.0]])]});}
            var Q30;
            {var subQ5=sQuery(id+"F0.wireOp",EDGE,"E512");Q30=makeQuery(id+"F0.imprint","IMPRINT",FACE,{"disambiguationData":[TD([[makeQuery(id+"F0.imprint","IMPRINT",EDGE,{"derivedFrom":subQ5}),-1.0]])]});}
            var Q31;
            {var subQ5=sQuery(id+"F0.wireOp",EDGE,"E476");Q31=makeQuery(id+"F0.imprint","IMPRINT",FACE,{"disambiguationData":[TD([[makeQuery(id+"F0.imprint","IMPRINT",EDGE,{"derivedFrom":subQ5}),-1.0]])]});}
            var Q32;
            {var subQ5=sQuery(id+"F0.wireOp",EDGE,"E395");Q32=makeQuery(id+"F0.imprint","IMPRINT",FACE,{"disambiguationData":[TD([[makeQuery(id+"F0.imprint","IMPRINT",EDGE,{"derivedFrom":subQ5}),-1.0]])]});}
            var Q33;
            {var subQ5=sQuery(id+"F0.wireOp",EDGE,"E413");Q33=makeQuery(id+"F0.imprint","IMPRINT",FACE,{"disambiguationData":[TD([[makeQuery(id+"F0.imprint","IMPRINT",EDGE,{"derivedFrom":subQ5}),-1.0]])]});}
            var Q34;
            {var subQ5=sQuery(id+"F0.wireOp",EDGE,"E422");Q34=makeQuery(id+"F0.imprint","IMPRINT",FACE,{"disambiguationData":[TD([[makeQuery(id+"F0.imprint","IMPRINT",EDGE,{"derivedFrom":subQ5}),-1.0]])]});}
            var Q35;
            {var subQ5=sQuery(id+"F0.wireOp",EDGE,"E521");Q35=makeQuery(id+"F0.imprint","IMPRINT",FACE,{"disambiguationData":[TD([[makeQuery(id+"F0.imprint","IMPRINT",EDGE,{"derivedFrom":subQ5}),-1.0]])]});}
            var Q36;
            {var subQ5=sQuery(id+"F0.wireOp",EDGE,"E440");Q36=makeQuery(id+"F0.imprint","IMPRINT",FACE,{"disambiguationData":[TD([[makeQuery(id+"F0.imprint","IMPRINT",EDGE,{"derivedFrom":subQ5}),-1.0]])]});}
            var Q37;
            {var subQ5=sQuery(id+"F0.wireOp",EDGE,"E530");Q37=makeQuery(id+"F0.imprint","IMPRINT",FACE,{"disambiguationData":[TD([[makeQuery(id+"F0.imprint","IMPRINT",EDGE,{"derivedFrom":subQ5}),-1.0]])]});}
            var Q38;
            {var subQ5=sQuery(id+"F0.wireOp",EDGE,"E458");Q38=makeQuery(id+"F0.imprint","IMPRINT",FACE,{"disambiguationData":[TD([[makeQuery(id+"F0.imprint","IMPRINT",EDGE,{"derivedFrom":subQ5}),-1.0]])]});}
            var Q39;
            {var subQ5=sQuery(id+"F0.wireOp",EDGE,"E485");Q39=makeQuery(id+"F0.imprint","IMPRINT",FACE,{"disambiguationData":[TD([[makeQuery(id+"F0.imprint","IMPRINT",EDGE,{"derivedFrom":subQ5}),-1.0]])]});}
            var Q40;
            {var subQ5=sQuery(id+"F0.wireOp",EDGE,"E467");Q40=makeQuery(id+"F0.imprint","IMPRINT",FACE,{"disambiguationData":[TD([[makeQuery(id+"F0.imprint","IMPRINT",EDGE,{"derivedFrom":subQ5}),-1.0]])]});}
            var Q41;
            {var subQ0=sQuery(id+"F0.wireOp",EDGE,"E528");Q41=makeQuery(id+"F0.imprint","IMPRINT",FACE,{"disambiguationData":[TD([[makeQuery(id+"F0.imprint","IMPRINT",EDGE,{"derivedFrom":subQ0}),-1.0]])]});}
            var Q42;
            {var subQ0=sQuery(id+"F0.wireOp",EDGE,"E402");Q42=makeQuery(id+"F0.imprint","IMPRINT",FACE,{"disambiguationData":[TD([[makeQuery(id+"F0.imprint","IMPRINT",EDGE,{"derivedFrom":subQ0}),-1.0]])]});}
            var Q43;
            {var subQ0=sQuery(id+"F0.wireOp",EDGE,"E492");Q43=makeQuery(id+"F0.imprint","IMPRINT",FACE,{"disambiguationData":[TD([[makeQuery(id+"F0.imprint","IMPRINT",EDGE,{"derivedFrom":subQ0}),-1.0]])]});}
            var Q44;
            {var subQ0=sQuery(id+"F0.wireOp",EDGE,"E474");Q44=makeQuery(id+"F0.imprint","IMPRINT",FACE,{"disambiguationData":[TD([[makeQuery(id+"F0.imprint","IMPRINT",EDGE,{"derivedFrom":subQ0}),-1.0]])]});}
            var Q45;
            {var subQ0=sQuery(id+"F0.wireOp",EDGE,"E546");Q45=makeQuery(id+"F0.imprint","IMPRINT",FACE,{"disambiguationData":[TD([[makeQuery(id+"F0.imprint","IMPRINT",EDGE,{"derivedFrom":subQ0}),-1.0]])]});}
            var Q46;
            {var subQ0=sQuery(id+"F0.wireOp",EDGE,"E420");Q46=makeQuery(id+"F0.imprint","IMPRINT",FACE,{"disambiguationData":[TD([[makeQuery(id+"F0.imprint","IMPRINT",EDGE,{"derivedFrom":subQ0}),-1.0]])]});}
            var Q47;
            {var subQ0=sQuery(id+"F0.wireOp",EDGE,"E465");Q47=makeQuery(id+"F0.imprint","IMPRINT",FACE,{"disambiguationData":[TD([[makeQuery(id+"F0.imprint","IMPRINT",EDGE,{"derivedFrom":subQ0}),-1.0]])]});}
            var Q48;
            {var subQ0=sQuery(id+"F0.wireOp",EDGE,"E456");Q48=makeQuery(id+"F0.imprint","IMPRINT",FACE,{"disambiguationData":[TD([[makeQuery(id+"F0.imprint","IMPRINT",EDGE,{"derivedFrom":subQ0}),-1.0]])]});}
            var Q49;
            {var subQ0=sQuery(id+"F0.wireOp",EDGE,"E519");Q49=makeQuery(id+"F0.imprint","IMPRINT",FACE,{"disambiguationData":[TD([[makeQuery(id+"F0.imprint","IMPRINT",EDGE,{"derivedFrom":subQ0}),-1.0]])]});}
            var Q50;
            {var subQ0=sQuery(id+"F0.wireOp",EDGE,"E384");Q50=makeQuery(id+"F0.imprint","IMPRINT",FACE,{"disambiguationData":[TD([[makeQuery(id+"F0.imprint","IMPRINT",EDGE,{"derivedFrom":subQ0}),-1.0]])]});}
            var Q51;
            {var subQ0=sQuery(id+"F0.wireOp",EDGE,"E447");Q51=makeQuery(id+"F0.imprint","IMPRINT",FACE,{"disambiguationData":[TD([[makeQuery(id+"F0.imprint","IMPRINT",EDGE,{"derivedFrom":subQ0}),-1.0]])]});}
            var Q52;
            {var subQ0=sQuery(id+"F0.wireOp",EDGE,"E555");Q52=makeQuery(id+"F0.imprint","IMPRINT",FACE,{"disambiguationData":[TD([[makeQuery(id+"F0.imprint","IMPRINT",EDGE,{"derivedFrom":subQ0}),-1.0]])]});}
            var Q53;
            {var subQ0=sQuery(id+"F0.wireOp",EDGE,"E510");Q53=makeQuery(id+"F0.imprint","IMPRINT",FACE,{"disambiguationData":[TD([[makeQuery(id+"F0.imprint","IMPRINT",EDGE,{"derivedFrom":subQ0}),-1.0]])]});}
            var Q54;
            {var subQ0=sQuery(id+"F0.wireOp",EDGE,"E537");Q54=makeQuery(id+"F0.imprint","IMPRINT",FACE,{"disambiguationData":[TD([[makeQuery(id+"F0.imprint","IMPRINT",EDGE,{"derivedFrom":subQ0}),-1.0]])]});}
            var Q55;
            {var subQ0=sQuery(id+"F0.wireOp",EDGE,"E429");Q55=makeQuery(id+"F0.imprint","IMPRINT",FACE,{"disambiguationData":[TD([[makeQuery(id+"F0.imprint","IMPRINT",EDGE,{"derivedFrom":subQ0}),-1.0]])]});}
            var Q56;
            {var subQ0=sQuery(id+"F0.wireOp",EDGE,"E438");Q56=makeQuery(id+"F0.imprint","IMPRINT",FACE,{"disambiguationData":[TD([[makeQuery(id+"F0.imprint","IMPRINT",EDGE,{"derivedFrom":subQ0}),-1.0]])]});}
            var Q57;
            {var subQ0=sQuery(id+"F0.wireOp",EDGE,"E393");Q57=makeQuery(id+"F0.imprint","IMPRINT",FACE,{"disambiguationData":[TD([[makeQuery(id+"F0.imprint","IMPRINT",EDGE,{"derivedFrom":subQ0}),-1.0]])]});}
            var Q58;
            {var subQ0=sQuery(id+"F0.wireOp",EDGE,"E501");Q58=makeQuery(id+"F0.imprint","IMPRINT",FACE,{"disambiguationData":[TD([[makeQuery(id+"F0.imprint","IMPRINT",EDGE,{"derivedFrom":subQ0}),-1.0]])]});}
            var Q59;
            {var subQ0=sQuery(id+"F0.wireOp",EDGE,"E411");Q59=makeQuery(id+"F0.imprint","IMPRINT",FACE,{"disambiguationData":[TD([[makeQuery(id+"F0.imprint","IMPRINT",EDGE,{"derivedFrom":subQ0}),-1.0]])]});}
            var Q60;
            {var subQ0=sQuery(id+"F0.wireOp",EDGE,"E483");Q60=makeQuery(id+"F0.imprint","IMPRINT",FACE,{"disambiguationData":[TD([[makeQuery(id+"F0.imprint","IMPRINT",EDGE,{"derivedFrom":subQ0}),-1.0]])]});}
            extrude(context, id + "F1", {"entities" : qUnion([Q0, Q1, Q2, Q3, Q4, Q5, Q6, Q7, Q8, Q9, Q10, Q11, Q12, Q13, Q14, Q15, Q16, Q17, Q18, Q19, Q20, Q21, Q22, Q23, Q24, Q25, Q26, Q27, Q28, Q29, Q30, Q31, Q32, Q33, Q34, Q35, Q36, Q37, Q38, Q39, Q40, Q41, Q42, Q43, Q44, Q45, Q46, Q47, Q48, Q49, Q50, Q51, Q52, Q53, Q54, Q55, Q56, Q57, Q58, Q59, Q60]), "depth" : 6.35 * mm});
        }
        {
            var Q0;
            {var subQ4=sQuery(id+"F0.wireOp",EDGE,"E285");Q0=makeQuery(id+"F0.imprint","IMPRINT",FACE,{"disambiguationData":[TD([[makeQuery(id+"F0.imprint","IMPRINT",EDGE,{"derivedFrom":subQ4}),-1.0]])]});}
            var Q1;
            {var subQ4=sQuery(id+"F0.wireOp",EDGE,"E348");Q1=makeQuery(id+"F0.imprint","IMPRINT",FACE,{"disambiguationData":[TD([[makeQuery(id+"F0.imprint","IMPRINT",EDGE,{"derivedFrom":subQ4}),-1.0]])]});}
            var Q2;
            {var subQ4=sQuery(id+"F0.wireOp",EDGE,"E159");Q2=makeQuery(id+"F0.imprint","IMPRINT",FACE,{"disambiguationData":[TD([[makeQuery(id+"F0.imprint","IMPRINT",EDGE,{"derivedFrom":subQ4}),-1.0]])]});}
            var Q3;
            {var subQ4=sQuery(id+"F0.wireOp",EDGE,"E267");Q3=makeQuery(id+"F0.imprint","IMPRINT",FACE,{"disambiguationData":[TD([[makeQuery(id+"F0.imprint","IMPRINT",EDGE,{"derivedFrom":subQ4}),-1.0]])]});}
            var Q4;
            {var subQ1=sQuery(id+"F0.wireOp",EDGE,"E33");Q4=makeQuery(id+"F0.imprint","IMPRINT",FACE,{"disambiguationData":[TD([[makeQuery(id+"F0.imprint","IMPRINT",EDGE,{"derivedFrom":subQ1}),-1.0]])]});}
            var Q5;
            {var subQ4=sQuery(id+"F0.wireOp",EDGE,"E6");Q5=makeQuery(id+"F0.imprint","IMPRINT",FACE,{"disambiguationData":[TD([[makeQuery(id+"F0.imprint","IMPRINT",EDGE,{"derivedFrom":subQ4}),-1.0]])]});}
            var Q6;
            {var subQ9=sQuery(id+"F0.wireOp",EDGE,"E231");Q6=makeQuery(id+"F0.imprint","IMPRINT",FACE,{"disambiguationData":[TD([[makeQuery(id+"F0.imprint","IMPRINT",EDGE,{"derivedFrom":subQ9}),-1.0]])]});}
            var Q7;
            {var subQ6=sQuery(id+"F0.wireOp",EDGE,"E303");Q7=makeQuery(id+"F0.imprint","IMPRINT",FACE,{"disambiguationData":[TD([[makeQuery(id+"F0.imprint","IMPRINT",EDGE,{"derivedFrom":subQ6}),-1.0]])]});}
            var Q8;
            {var subQ1=sQuery(id+"F0.wireOp",EDGE,"E168");Q8=makeQuery(id+"F0.imprint","IMPRINT",FACE,{"disambiguationData":[TD([[makeQuery(id+"F0.imprint","IMPRINT",EDGE,{"derivedFrom":subQ1}),-1.0]])]});}
            var Q9;
            {var subQ4=sQuery(id+"F0.wireOp",EDGE,"E114");Q9=makeQuery(id+"F0.imprint","IMPRINT",FACE,{"disambiguationData":[TD([[makeQuery(id+"F0.imprint","IMPRINT",EDGE,{"derivedFrom":subQ4}),-1.0]])]});}
            var Q10;
            {var subQ9=sQuery(id+"F0.wireOp",EDGE,"E96");Q10=makeQuery(id+"F0.imprint","IMPRINT",FACE,{"disambiguationData":[TD([[makeQuery(id+"F0.imprint","IMPRINT",EDGE,{"derivedFrom":subQ9}),-1.0]])]});}
            var Q11;
            {var subQ1=sQuery(id+"F0.wireOp",EDGE,"E375");Q11=makeQuery(id+"F0.imprint","IMPRINT",FACE,{"disambiguationData":[TD([[makeQuery(id+"F0.imprint","IMPRINT",EDGE,{"derivedFrom":subQ1}),-1.0]])]});}
            var Q12;
            {var subQ4=sQuery(id+"F0.wireOp",EDGE,"E177");Q12=makeQuery(id+"F0.imprint","IMPRINT",FACE,{"disambiguationData":[TD([[makeQuery(id+"F0.imprint","IMPRINT",EDGE,{"derivedFrom":subQ4}),-1.0]])]});}
            var Q13;
            {var subQ9=sQuery(id+"F0.wireOp",EDGE,"E330");Q13=makeQuery(id+"F0.imprint","IMPRINT",FACE,{"disambiguationData":[TD([[makeQuery(id+"F0.imprint","IMPRINT",EDGE,{"derivedFrom":subQ9}),-1.0]])]});}
            var Q14;
            {var subQ1=sQuery(id+"F0.wireOp",EDGE,"E213");Q14=makeQuery(id+"F0.imprint","IMPRINT",FACE,{"disambiguationData":[TD([[makeQuery(id+"F0.imprint","IMPRINT",EDGE,{"derivedFrom":subQ1}),-1.0]])]});}
            var Q15;
            {var subQ4=sQuery(id+"F0.wireOp",EDGE,"E195");Q15=makeQuery(id+"F0.imprint","IMPRINT",FACE,{"disambiguationData":[TD([[makeQuery(id+"F0.imprint","IMPRINT",EDGE,{"derivedFrom":subQ4}),-1.0]])]});}
            var Q16;
            {var subQ4=sQuery(id+"F0.wireOp",EDGE,"E105");Q16=makeQuery(id+"F0.imprint","IMPRINT",FACE,{"disambiguationData":[TD([[makeQuery(id+"F0.imprint","IMPRINT",EDGE,{"derivedFrom":subQ4}),-1.0]])]});}
            var Q17;
            {var subQ1=sQuery(id+"F0.wireOp",EDGE,"E78");Q17=makeQuery(id+"F0.imprint","IMPRINT",FACE,{"disambiguationData":[TD([[makeQuery(id+"F0.imprint","IMPRINT",EDGE,{"derivedFrom":subQ1}),-1.0]])]});}
            var Q18;
            {var subQ4=sQuery(id+"F0.wireOp",EDGE,"E186");Q18=makeQuery(id+"F0.imprint","IMPRINT",FACE,{"disambiguationData":[TD([[makeQuery(id+"F0.imprint","IMPRINT",EDGE,{"derivedFrom":subQ4}),-1.0]])]});}
            var Q19;
            {var subQ4=sQuery(id+"F0.wireOp",EDGE,"E339");Q19=makeQuery(id+"F0.imprint","IMPRINT",FACE,{"disambiguationData":[TD([[makeQuery(id+"F0.imprint","IMPRINT",EDGE,{"derivedFrom":subQ4}),-1.0]])]});}
            var Q20;
            {var subQ4=sQuery(id+"F0.wireOp",EDGE,"E312");Q20=makeQuery(id+"F0.imprint","IMPRINT",FACE,{"disambiguationData":[TD([[makeQuery(id+"F0.imprint","IMPRINT",EDGE,{"derivedFrom":subQ4}),-1.0]])]});}
            var Q21;
            {var subQ1=sQuery(id+"F0.wireOp",EDGE,"E123");Q21=makeQuery(id+"F0.imprint","IMPRINT",FACE,{"disambiguationData":[TD([[makeQuery(id+"F0.imprint","IMPRINT",EDGE,{"derivedFrom":subQ1}),-1.0]])]});}
            var Q22;
            {var subQ4=sQuery(id+"F0.wireOp",EDGE,"E69");Q22=makeQuery(id+"F0.imprint","IMPRINT",FACE,{"disambiguationData":[TD([[makeQuery(id+"F0.imprint","IMPRINT",EDGE,{"derivedFrom":subQ4}),-1.0]])]});}
            var Q23;
            {var subQ4=sQuery(id+"F0.wireOp",EDGE,"E249");Q23=makeQuery(id+"F0.imprint","IMPRINT",FACE,{"disambiguationData":[TD([[makeQuery(id+"F0.imprint","IMPRINT",EDGE,{"derivedFrom":subQ4}),-1.0]])]});}
            var Q24;
            {var subQ4=sQuery(id+"F0.wireOp",EDGE,"E276");Q24=makeQuery(id+"F0.imprint","IMPRINT",FACE,{"disambiguationData":[TD([[makeQuery(id+"F0.imprint","IMPRINT",EDGE,{"derivedFrom":subQ4}),-1.0]])]});}
            var Q25;
            {var subQ1=sQuery(id+"F0.wireOp",EDGE,"E258");Q25=makeQuery(id+"F0.imprint","IMPRINT",FACE,{"disambiguationData":[TD([[makeQuery(id+"F0.imprint","IMPRINT",EDGE,{"derivedFrom":subQ1}),-1.0]])]});}
            var Q26;
            {var subQ4=sQuery(id+"F0.wireOp",EDGE,"E51");Q26=makeQuery(id+"F0.imprint","IMPRINT",FACE,{"disambiguationData":[TD([[makeQuery(id+"F0.imprint","IMPRINT",EDGE,{"derivedFrom":subQ4}),-1.0]])]});}
            var Q27;
            {var subQ4=sQuery(id+"F0.wireOp",EDGE,"E87");Q27=makeQuery(id+"F0.imprint","IMPRINT",FACE,{"disambiguationData":[TD([[makeQuery(id+"F0.imprint","IMPRINT",EDGE,{"derivedFrom":subQ4}),-1.0]])]});}
            var Q28;
            {var subQ4=sQuery(id+"F0.wireOp",EDGE,"E42");Q28=makeQuery(id+"F0.imprint","IMPRINT",FACE,{"disambiguationData":[TD([[makeQuery(id+"F0.imprint","IMPRINT",EDGE,{"derivedFrom":subQ4}),-1.0]])]});}
            var Q29;
            {var subQ4=sQuery(id+"F0.wireOp",EDGE,"E141");Q29=makeQuery(id+"F0.imprint","IMPRINT",FACE,{"disambiguationData":[TD([[makeQuery(id+"F0.imprint","IMPRINT",EDGE,{"derivedFrom":subQ4}),-1.0]])]});}
            var Q30;
            {var subQ4=sQuery(id+"F0.wireOp",EDGE,"E366");Q30=makeQuery(id+"F0.imprint","IMPRINT",FACE,{"disambiguationData":[TD([[makeQuery(id+"F0.imprint","IMPRINT",EDGE,{"derivedFrom":subQ4}),-1.0]])]});}
            var Q31;
            {var subQ4=sQuery(id+"F0.wireOp",EDGE,"E357");Q31=makeQuery(id+"F0.imprint","IMPRINT",FACE,{"disambiguationData":[TD([[makeQuery(id+"F0.imprint","IMPRINT",EDGE,{"derivedFrom":subQ4}),-1.0]])]});}
            var Q32;
            {var subQ1=sQuery(id+"F0.wireOp",EDGE,"E204");Q32=makeQuery(id+"F0.imprint","IMPRINT",FACE,{"disambiguationData":[TD([[makeQuery(id+"F0.imprint","IMPRINT",EDGE,{"derivedFrom":subQ1}),-1.0]])]});}
            var Q33;
            {var subQ4=sQuery(id+"F0.wireOp",EDGE,"E321");Q33=makeQuery(id+"F0.imprint","IMPRINT",FACE,{"disambiguationData":[TD([[makeQuery(id+"F0.imprint","IMPRINT",EDGE,{"derivedFrom":subQ4}),-1.0]])]});}
            var Q34;
            {var subQ1=sQuery(id+"F0.wireOp",EDGE,"E222");Q34=makeQuery(id+"F0.imprint","IMPRINT",FACE,{"disambiguationData":[TD([[makeQuery(id+"F0.imprint","IMPRINT",EDGE,{"derivedFrom":subQ1}),-1.0]])]});}
            var Q35;
            Q35=makeQuery(id+"F0.imprint","IMPRINT",FACE,{"disambiguationData":[TD([[makeQuery(id+"F0.imprint","IMPRINT",EDGE,{"derivedFrom":sQuery(id+"F0.wireOp",EDGE,"E2")}),-1.0]])]});
            var Q36;
            {var subQ1=sQuery(id+"F0.wireOp",EDGE,"E294");Q36=makeQuery(id+"F0.imprint","IMPRINT",FACE,{"disambiguationData":[TD([[makeQuery(id+"F0.imprint","IMPRINT",EDGE,{"derivedFrom":subQ1}),-1.0]])]});}
            var Q37;
            {var subQ4=sQuery(id+"F0.wireOp",EDGE,"E150");Q37=makeQuery(id+"F0.imprint","IMPRINT",FACE,{"disambiguationData":[TD([[makeQuery(id+"F0.imprint","IMPRINT",EDGE,{"derivedFrom":subQ4}),-1.0]])]});}
            var Q38;
            {var subQ4=sQuery(id+"F0.wireOp",EDGE,"E132");Q38=makeQuery(id+"F0.imprint","IMPRINT",FACE,{"disambiguationData":[TD([[makeQuery(id+"F0.imprint","IMPRINT",EDGE,{"derivedFrom":subQ4}),-1.0]])]});}
            var Q39;
            {var subQ4=sQuery(id+"F0.wireOp",EDGE,"E60");Q39=makeQuery(id+"F0.imprint","IMPRINT",FACE,{"disambiguationData":[TD([[makeQuery(id+"F0.imprint","IMPRINT",EDGE,{"derivedFrom":subQ4}),-1.0]])]});}
            var Q40;
            {var subQ4=sQuery(id+"F0.wireOp",EDGE,"E240");Q40=makeQuery(id+"F0.imprint","IMPRINT",FACE,{"disambiguationData":[TD([[makeQuery(id+"F0.imprint","IMPRINT",EDGE,{"derivedFrom":subQ4}),-1.0]])]});}
            var Q41;
            {var subQ5=sQuery(id+"F0.wireOp",EDGE,"E52");Q41=makeQuery(id+"F0.imprint","IMPRINT",FACE,{"disambiguationData":[TD([[makeQuery(id+"F0.imprint","IMPRINT",EDGE,{"derivedFrom":subQ5}),-1.0]])]});}
            var Q42;
            {var subQ5=sQuery(id+"F0.wireOp",EDGE,"E88");Q42=makeQuery(id+"F0.imprint","IMPRINT",FACE,{"disambiguationData":[TD([[makeQuery(id+"F0.imprint","IMPRINT",EDGE,{"derivedFrom":subQ5}),-1.0]])]});}
            var Q43;
            {var subQ5=sQuery(id+"F0.wireOp",EDGE,"E250");Q43=makeQuery(id+"F0.imprint","IMPRINT",FACE,{"disambiguationData":[TD([[makeQuery(id+"F0.imprint","IMPRINT",EDGE,{"derivedFrom":subQ5}),-1.0]])]});}
            var Q44;
            {var subQ5=sQuery(id+"F0.wireOp",EDGE,"E133");Q44=makeQuery(id+"F0.imprint","IMPRINT",FACE,{"disambiguationData":[TD([[makeQuery(id+"F0.imprint","IMPRINT",EDGE,{"derivedFrom":subQ5}),-1.0]])]});}
            var Q45;
            {var subQ5=sQuery(id+"F0.wireOp",EDGE,"E313");Q45=makeQuery(id+"F0.imprint","IMPRINT",FACE,{"disambiguationData":[TD([[makeQuery(id+"F0.imprint","IMPRINT",EDGE,{"derivedFrom":subQ5}),-1.0]])]});}
            var Q46;
            {var subQ5=sQuery(id+"F0.wireOp",EDGE,"E43");Q46=makeQuery(id+"F0.imprint","IMPRINT",FACE,{"disambiguationData":[TD([[makeQuery(id+"F0.imprint","IMPRINT",EDGE,{"derivedFrom":subQ5}),-1.0]])]});}
            var Q47;
            {var subQ5=sQuery(id+"F0.wireOp",EDGE,"E259");Q47=makeQuery(id+"F0.imprint","IMPRINT",FACE,{"disambiguationData":[TD([[makeQuery(id+"F0.imprint","IMPRINT",EDGE,{"derivedFrom":subQ5}),-1.0]])]});}
            var Q48;
            {var subQ5=sQuery(id+"F0.wireOp",EDGE,"E286");Q48=makeQuery(id+"F0.imprint","IMPRINT",FACE,{"disambiguationData":[TD([[makeQuery(id+"F0.imprint","IMPRINT",EDGE,{"derivedFrom":subQ5}),-1.0]])]});}
            var Q49;
            {var subQ5=sQuery(id+"F0.wireOp",EDGE,"E79");Q49=makeQuery(id+"F0.imprint","IMPRINT",FACE,{"disambiguationData":[TD([[makeQuery(id+"F0.imprint","IMPRINT",EDGE,{"derivedFrom":subQ5}),-1.0]])]});}
            var Q50;
            {var subQ5=sQuery(id+"F0.wireOp",EDGE,"E304");Q50=makeQuery(id+"F0.imprint","IMPRINT",FACE,{"disambiguationData":[TD([[makeQuery(id+"F0.imprint","IMPRINT",EDGE,{"derivedFrom":subQ5}),-1.0]])]});}
            var Q51;
            {var subQ5=sQuery(id+"F0.wireOp",EDGE,"E160");Q51=makeQuery(id+"F0.imprint","IMPRINT",FACE,{"disambiguationData":[TD([[makeQuery(id+"F0.imprint","IMPRINT",EDGE,{"derivedFrom":subQ5}),-1.0]])]});}
            var Q52;
            {var subQ5=sQuery(id+"F0.wireOp",EDGE,"E97");Q52=makeQuery(id+"F0.imprint","IMPRINT",FACE,{"disambiguationData":[TD([[makeQuery(id+"F0.imprint","IMPRINT",EDGE,{"derivedFrom":subQ5}),-1.0]])]});}
            var Q53;
            {var subQ5=sQuery(id+"F0.wireOp",EDGE,"E169");Q53=makeQuery(id+"F0.imprint","IMPRINT",FACE,{"disambiguationData":[TD([[makeQuery(id+"F0.imprint","IMPRINT",EDGE,{"derivedFrom":subQ5}),-1.0]])]});}
            var Q54;
            {var subQ5=sQuery(id+"F0.wireOp",EDGE,"E196");Q54=makeQuery(id+"F0.imprint","IMPRINT",FACE,{"disambiguationData":[TD([[makeQuery(id+"F0.imprint","IMPRINT",EDGE,{"derivedFrom":subQ5}),-1.0]])]});}
            var Q55;
            {var subQ5=sQuery(id+"F0.wireOp",EDGE,"E205");Q55=makeQuery(id+"F0.imprint","IMPRINT",FACE,{"disambiguationData":[TD([[makeQuery(id+"F0.imprint","IMPRINT",EDGE,{"derivedFrom":subQ5}),-1.0]])]});}
            var Q56;
            {var subQ5=sQuery(id+"F0.wireOp",EDGE,"E331");Q56=makeQuery(id+"F0.imprint","IMPRINT",FACE,{"disambiguationData":[TD([[makeQuery(id+"F0.imprint","IMPRINT",EDGE,{"derivedFrom":subQ5}),-1.0]])]});}
            var Q57;
            {var subQ5=sQuery(id+"F0.wireOp",EDGE,"E241");Q57=makeQuery(id+"F0.imprint","IMPRINT",FACE,{"disambiguationData":[TD([[makeQuery(id+"F0.imprint","IMPRINT",EDGE,{"derivedFrom":subQ5}),-1.0]])]});}
            var Q58;
            {var subQ5=sQuery(id+"F0.wireOp",EDGE,"E7");Q58=makeQuery(id+"F0.imprint","IMPRINT",FACE,{"disambiguationData":[TD([[makeQuery(id+"F0.imprint","IMPRINT",EDGE,{"derivedFrom":subQ5}),-1.0]])]});}
            var Q59;
            {var subQ5=sQuery(id+"F0.wireOp",EDGE,"E268");Q59=makeQuery(id+"F0.imprint","IMPRINT",FACE,{"disambiguationData":[TD([[makeQuery(id+"F0.imprint","IMPRINT",EDGE,{"derivedFrom":subQ5}),-1.0]])]});}
            var Q60;
            {var subQ5=sQuery(id+"F0.wireOp",EDGE,"E358");Q60=makeQuery(id+"F0.imprint","IMPRINT",FACE,{"disambiguationData":[TD([[makeQuery(id+"F0.imprint","IMPRINT",EDGE,{"derivedFrom":subQ5}),-1.0]])]});}
            var Q61;
            {var subQ5=sQuery(id+"F0.wireOp",EDGE,"E61");Q61=makeQuery(id+"F0.imprint","IMPRINT",FACE,{"disambiguationData":[TD([[makeQuery(id+"F0.imprint","IMPRINT",EDGE,{"derivedFrom":subQ5}),-1.0]])]});}
            var Q62;
            {var subQ5=sQuery(id+"F0.wireOp",EDGE,"E277");Q62=makeQuery(id+"F0.imprint","IMPRINT",FACE,{"disambiguationData":[TD([[makeQuery(id+"F0.imprint","IMPRINT",EDGE,{"derivedFrom":subQ5}),-1.0]])]});}
            var Q63;
            {var subQ5=sQuery(id+"F0.wireOp",EDGE,"E142");Q63=makeQuery(id+"F0.imprint","IMPRINT",FACE,{"disambiguationData":[TD([[makeQuery(id+"F0.imprint","IMPRINT",EDGE,{"derivedFrom":subQ5}),-1.0]])]});}
            var Q64;
            {var subQ5=sQuery(id+"F0.wireOp",EDGE,"E214");Q64=makeQuery(id+"F0.imprint","IMPRINT",FACE,{"disambiguationData":[TD([[makeQuery(id+"F0.imprint","IMPRINT",EDGE,{"derivedFrom":subQ5}),-1.0]])]});}
            var Q65;
            {var subQ5=sQuery(id+"F0.wireOp",EDGE,"E232");Q65=makeQuery(id+"F0.imprint","IMPRINT",FACE,{"disambiguationData":[TD([[makeQuery(id+"F0.imprint","IMPRINT",EDGE,{"derivedFrom":subQ5}),-1.0]])]});}
            var Q66;
            {var subQ5=sQuery(id+"F0.wireOp",EDGE,"E151");Q66=makeQuery(id+"F0.imprint","IMPRINT",FACE,{"disambiguationData":[TD([[makeQuery(id+"F0.imprint","IMPRINT",EDGE,{"derivedFrom":subQ5}),-1.0]])]});}
            var Q67;
            {var subQ5=sQuery(id+"F0.wireOp",EDGE,"E340");Q67=makeQuery(id+"F0.imprint","IMPRINT",FACE,{"disambiguationData":[TD([[makeQuery(id+"F0.imprint","IMPRINT",EDGE,{"derivedFrom":subQ5}),-1.0]])]});}
            var Q68;
            {var subQ5=sQuery(id+"F0.wireOp",EDGE,"E349");Q68=makeQuery(id+"F0.imprint","IMPRINT",FACE,{"disambiguationData":[TD([[makeQuery(id+"F0.imprint","IMPRINT",EDGE,{"derivedFrom":subQ5}),-1.0]])]});}
            var Q69;
            {var subQ5=sQuery(id+"F0.wireOp",EDGE,"E178");Q69=makeQuery(id+"F0.imprint","IMPRINT",FACE,{"disambiguationData":[TD([[makeQuery(id+"F0.imprint","IMPRINT",EDGE,{"derivedFrom":subQ5}),-1.0]])]});}
            var Q70;
            {var subQ5=sQuery(id+"F0.wireOp",EDGE,"E106");Q70=makeQuery(id+"F0.imprint","IMPRINT",FACE,{"disambiguationData":[TD([[makeQuery(id+"F0.imprint","IMPRINT",EDGE,{"derivedFrom":subQ5}),-1.0]])]});}
            var Q71;
            {var subQ5=sQuery(id+"F0.wireOp",EDGE,"E376");Q71=makeQuery(id+"F0.imprint","IMPRINT",FACE,{"disambiguationData":[TD([[makeQuery(id+"F0.imprint","IMPRINT",EDGE,{"derivedFrom":subQ5}),-1.0]])]});}
            var Q72;
            {var subQ5=sQuery(id+"F0.wireOp",EDGE,"E124");Q72=makeQuery(id+"F0.imprint","IMPRINT",FACE,{"disambiguationData":[TD([[makeQuery(id+"F0.imprint","IMPRINT",EDGE,{"derivedFrom":subQ5}),-1.0]])]});}
            var Q73;
            {var subQ5=sQuery(id+"F0.wireOp",EDGE,"E367");Q73=makeQuery(id+"F0.imprint","IMPRINT",FACE,{"disambiguationData":[TD([[makeQuery(id+"F0.imprint","IMPRINT",EDGE,{"derivedFrom":subQ5}),-1.0]])]});}
            var Q74;
            {var subQ5=sQuery(id+"F0.wireOp",EDGE,"E223");Q74=makeQuery(id+"F0.imprint","IMPRINT",FACE,{"disambiguationData":[TD([[makeQuery(id+"F0.imprint","IMPRINT",EDGE,{"derivedFrom":subQ5}),-1.0]])]});}
            var Q75;
            {var subQ5=sQuery(id+"F0.wireOp",EDGE,"E322");Q75=makeQuery(id+"F0.imprint","IMPRINT",FACE,{"disambiguationData":[TD([[makeQuery(id+"F0.imprint","IMPRINT",EDGE,{"derivedFrom":subQ5}),-1.0]])]});}
            var Q76;
            {var subQ5=sQuery(id+"F0.wireOp",EDGE,"E187");Q76=makeQuery(id+"F0.imprint","IMPRINT",FACE,{"disambiguationData":[TD([[makeQuery(id+"F0.imprint","IMPRINT",EDGE,{"derivedFrom":subQ5}),-1.0]])]});}
            var Q77;
            {var subQ5=sQuery(id+"F0.wireOp",EDGE,"E115");Q77=makeQuery(id+"F0.imprint","IMPRINT",FACE,{"disambiguationData":[TD([[makeQuery(id+"F0.imprint","IMPRINT",EDGE,{"derivedFrom":subQ5}),-1.0]])]});}
            var Q78;
            {var subQ5=sQuery(id+"F0.wireOp",EDGE,"E34");Q78=makeQuery(id+"F0.imprint","IMPRINT",FACE,{"disambiguationData":[TD([[makeQuery(id+"F0.imprint","IMPRINT",EDGE,{"derivedFrom":subQ5}),-1.0]])]});}
            var Q79;
            {var subQ5=sQuery(id+"F0.wireOp",EDGE,"E70");Q79=makeQuery(id+"F0.imprint","IMPRINT",FACE,{"disambiguationData":[TD([[makeQuery(id+"F0.imprint","IMPRINT",EDGE,{"derivedFrom":subQ5}),-1.0]])]});}
            var Q80;
            {var subQ0=sQuery(id+"F0.wireOp",EDGE,"E77");Q80=makeQuery(id+"F0.imprint","IMPRINT",FACE,{"disambiguationData":[TD([[makeQuery(id+"F0.imprint","IMPRINT",EDGE,{"derivedFrom":subQ0}),-1.0]])]});}
            var Q81;
            {var subQ0=sQuery(id+"F0.wireOp",EDGE,"E5");Q81=makeQuery(id+"F0.imprint","IMPRINT",FACE,{"disambiguationData":[TD([[makeQuery(id+"F0.imprint","IMPRINT",EDGE,{"derivedFrom":subQ0}),-1.0]])]});}
            var Q82;
            {var subQ0=sQuery(id+"F0.wireOp",EDGE,"E95");Q82=makeQuery(id+"F0.imprint","IMPRINT",FACE,{"disambiguationData":[TD([[makeQuery(id+"F0.imprint","IMPRINT",EDGE,{"derivedFrom":subQ0}),-1.0]])]});}
            var Q83;
            {var subQ0=sQuery(id+"F0.wireOp",EDGE,"E185");Q83=makeQuery(id+"F0.imprint","IMPRINT",FACE,{"disambiguationData":[TD([[makeQuery(id+"F0.imprint","IMPRINT",EDGE,{"derivedFrom":subQ0}),-1.0]])]});}
            var Q84;
            {var subQ5=sQuery(id+"F0.wireOp",EDGE,"E295");Q84=makeQuery(id+"F0.imprint","IMPRINT",FACE,{"disambiguationData":[TD([[makeQuery(id+"F0.imprint","IMPRINT",EDGE,{"derivedFrom":subQ5}),-1.0]])]});}
            var Q85;
            {var subQ0=sQuery(id+"F0.wireOp",EDGE,"E365");Q85=makeQuery(id+"F0.imprint","IMPRINT",FACE,{"disambiguationData":[TD([[makeQuery(id+"F0.imprint","IMPRINT",EDGE,{"derivedFrom":subQ0}),-1.0]])]});}
            var Q86;
            {var subQ0=sQuery(id+"F0.wireOp",EDGE,"E68");Q86=makeQuery(id+"F0.imprint","IMPRINT",FACE,{"disambiguationData":[TD([[makeQuery(id+"F0.imprint","IMPRINT",EDGE,{"derivedFrom":subQ0}),-1.0]])]});}
            var Q87;
            {var subQ0=sQuery(id+"F0.wireOp",EDGE,"E230");Q87=makeQuery(id+"F0.imprint","IMPRINT",FACE,{"disambiguationData":[TD([[makeQuery(id+"F0.imprint","IMPRINT",EDGE,{"derivedFrom":subQ0}),-1.0]])]});}
            var Q88;
            {var subQ0=sQuery(id+"F0.wireOp",EDGE,"E158");Q88=makeQuery(id+"F0.imprint","IMPRINT",FACE,{"disambiguationData":[TD([[makeQuery(id+"F0.imprint","IMPRINT",EDGE,{"derivedFrom":subQ0}),-1.0]])]});}
            var Q89;
            {var subQ0=sQuery(id+"F0.wireOp",EDGE,"E212");Q89=makeQuery(id+"F0.imprint","IMPRINT",FACE,{"disambiguationData":[TD([[makeQuery(id+"F0.imprint","IMPRINT",EDGE,{"derivedFrom":subQ0}),-1.0]])]});}
            var Q90;
            {var subQ0=sQuery(id+"F0.wireOp",EDGE,"E347");Q90=makeQuery(id+"F0.imprint","IMPRINT",FACE,{"disambiguationData":[TD([[makeQuery(id+"F0.imprint","IMPRINT",EDGE,{"derivedFrom":subQ0}),-1.0]])]});}
            var Q91;
            {var subQ0=sQuery(id+"F0.wireOp",EDGE,"E275");Q91=makeQuery(id+"F0.imprint","IMPRINT",FACE,{"disambiguationData":[TD([[makeQuery(id+"F0.imprint","IMPRINT",EDGE,{"derivedFrom":subQ0}),-1.0]])]});}
            var Q92;
            {var subQ0=sQuery(id+"F0.wireOp",EDGE,"E41");Q92=makeQuery(id+"F0.imprint","IMPRINT",FACE,{"disambiguationData":[TD([[makeQuery(id+"F0.imprint","IMPRINT",EDGE,{"derivedFrom":subQ0}),-1.0]])]});}
            var Q93;
            {var subQ0=sQuery(id+"F0.wireOp",EDGE,"E86");Q93=makeQuery(id+"F0.imprint","IMPRINT",FACE,{"disambiguationData":[TD([[makeQuery(id+"F0.imprint","IMPRINT",EDGE,{"derivedFrom":subQ0}),-1.0]])]});}
            var Q94;
            {var subQ0=sQuery(id+"F0.wireOp",EDGE,"E104");Q94=makeQuery(id+"F0.imprint","IMPRINT",FACE,{"disambiguationData":[TD([[makeQuery(id+"F0.imprint","IMPRINT",EDGE,{"derivedFrom":subQ0}),-1.0]])]});}
            var Q95;
            {var subQ0=sQuery(id+"F0.wireOp",EDGE,"E113");Q95=makeQuery(id+"F0.imprint","IMPRINT",FACE,{"disambiguationData":[TD([[makeQuery(id+"F0.imprint","IMPRINT",EDGE,{"derivedFrom":subQ0}),-1.0]])]});}
            var Q96;
            {var subQ0=sQuery(id+"F0.wireOp",EDGE,"E338");Q96=makeQuery(id+"F0.imprint","IMPRINT",FACE,{"disambiguationData":[TD([[makeQuery(id+"F0.imprint","IMPRINT",EDGE,{"derivedFrom":subQ0}),-1.0]])]});}
            var Q97;
            {var subQ0=sQuery(id+"F0.wireOp",EDGE,"E356");Q97=makeQuery(id+"F0.imprint","IMPRINT",FACE,{"disambiguationData":[TD([[makeQuery(id+"F0.imprint","IMPRINT",EDGE,{"derivedFrom":subQ0}),-1.0]])]});}
            var Q98;
            {var subQ0=sQuery(id+"F0.wireOp",EDGE,"E194");Q98=makeQuery(id+"F0.imprint","IMPRINT",FACE,{"disambiguationData":[TD([[makeQuery(id+"F0.imprint","IMPRINT",EDGE,{"derivedFrom":subQ0}),-1.0]])]});}
            var Q99;
            {var subQ0=sQuery(id+"F0.wireOp",EDGE,"E329");Q99=makeQuery(id+"F0.imprint","IMPRINT",FACE,{"disambiguationData":[TD([[makeQuery(id+"F0.imprint","IMPRINT",EDGE,{"derivedFrom":subQ0}),-1.0]])]});}
            var Q100;
            {var subQ0=sQuery(id+"F0.wireOp",EDGE,"E311");Q100=makeQuery(id+"F0.imprint","IMPRINT",FACE,{"disambiguationData":[TD([[makeQuery(id+"F0.imprint","IMPRINT",EDGE,{"derivedFrom":subQ0}),-1.0]])]});}
            var Q101;
            {var subQ0=sQuery(id+"F0.wireOp",EDGE,"E149");Q101=makeQuery(id+"F0.imprint","IMPRINT",FACE,{"disambiguationData":[TD([[makeQuery(id+"F0.imprint","IMPRINT",EDGE,{"derivedFrom":subQ0}),-1.0]])]});}
            var Q102;
            {var subQ0=sQuery(id+"F0.wireOp",EDGE,"E32");Q102=makeQuery(id+"F0.imprint","IMPRINT",FACE,{"disambiguationData":[TD([[makeQuery(id+"F0.imprint","IMPRINT",EDGE,{"derivedFrom":subQ0}),-1.0]])]});}
            var Q103;
            {var subQ0=sQuery(id+"F0.wireOp",EDGE,"E59");Q103=makeQuery(id+"F0.imprint","IMPRINT",FACE,{"disambiguationData":[TD([[makeQuery(id+"F0.imprint","IMPRINT",EDGE,{"derivedFrom":subQ0}),-1.0]])]});}
            var Q104;
            {var subQ0=sQuery(id+"F0.wireOp",EDGE,"E221");Q104=makeQuery(id+"F0.imprint","IMPRINT",FACE,{"disambiguationData":[TD([[makeQuery(id+"F0.imprint","IMPRINT",EDGE,{"derivedFrom":subQ0}),-1.0]])]});}
            var Q105;
            {var subQ0=sQuery(id+"F0.wireOp",EDGE,"E266");Q105=makeQuery(id+"F0.imprint","IMPRINT",FACE,{"disambiguationData":[TD([[makeQuery(id+"F0.imprint","IMPRINT",EDGE,{"derivedFrom":subQ0}),-1.0]])]});}
            var Q106;
            {var subQ0=sQuery(id+"F0.wireOp",EDGE,"E239");Q106=makeQuery(id+"F0.imprint","IMPRINT",FACE,{"disambiguationData":[TD([[makeQuery(id+"F0.imprint","IMPRINT",EDGE,{"derivedFrom":subQ0}),-1.0]])]});}
            var Q107;
            {var subQ0=sQuery(id+"F0.wireOp",EDGE,"E176");Q107=makeQuery(id+"F0.imprint","IMPRINT",FACE,{"disambiguationData":[TD([[makeQuery(id+"F0.imprint","IMPRINT",EDGE,{"derivedFrom":subQ0}),-1.0]])]});}
            var Q108;
            {var subQ0=sQuery(id+"F0.wireOp",EDGE,"E131");Q108=makeQuery(id+"F0.imprint","IMPRINT",FACE,{"disambiguationData":[TD([[makeQuery(id+"F0.imprint","IMPRINT",EDGE,{"derivedFrom":subQ0}),-1.0]])]});}
            var Q109;
            {var subQ0=sQuery(id+"F0.wireOp",EDGE,"E203");Q109=makeQuery(id+"F0.imprint","IMPRINT",FACE,{"disambiguationData":[TD([[makeQuery(id+"F0.imprint","IMPRINT",EDGE,{"derivedFrom":subQ0}),-1.0]])]});}
            var Q110;
            {var subQ0=sQuery(id+"F0.wireOp",EDGE,"E248");Q110=makeQuery(id+"F0.imprint","IMPRINT",FACE,{"disambiguationData":[TD([[makeQuery(id+"F0.imprint","IMPRINT",EDGE,{"derivedFrom":subQ0}),-1.0]])]});}
            var Q111;
            {var subQ0=sQuery(id+"F0.wireOp",EDGE,"E284");Q111=makeQuery(id+"F0.imprint","IMPRINT",FACE,{"disambiguationData":[TD([[makeQuery(id+"F0.imprint","IMPRINT",EDGE,{"derivedFrom":subQ0}),-1.0]])]});}
            var Q112;
            {var subQ0=sQuery(id+"F0.wireOp",EDGE,"E257");Q112=makeQuery(id+"F0.imprint","IMPRINT",FACE,{"disambiguationData":[TD([[makeQuery(id+"F0.imprint","IMPRINT",EDGE,{"derivedFrom":subQ0}),-1.0]])]});}
            var Q113;
            {var subQ0=sQuery(id+"F0.wireOp",EDGE,"E293");Q113=makeQuery(id+"F0.imprint","IMPRINT",FACE,{"disambiguationData":[TD([[makeQuery(id+"F0.imprint","IMPRINT",EDGE,{"derivedFrom":subQ0}),-1.0]])]});}
            var Q114;
            {var subQ0=sQuery(id+"F0.wireOp",EDGE,"E167");Q114=makeQuery(id+"F0.imprint","IMPRINT",FACE,{"disambiguationData":[TD([[makeQuery(id+"F0.imprint","IMPRINT",EDGE,{"derivedFrom":subQ0}),-1.0]])]});}
            var Q115;
            {var subQ0=sQuery(id+"F0.wireOp",EDGE,"E320");Q115=makeQuery(id+"F0.imprint","IMPRINT",FACE,{"disambiguationData":[TD([[makeQuery(id+"F0.imprint","IMPRINT",EDGE,{"derivedFrom":subQ0}),-1.0]])]});}
            var Q116;
            {var subQ0=sQuery(id+"F0.wireOp",EDGE,"E122");Q116=makeQuery(id+"F0.imprint","IMPRINT",FACE,{"disambiguationData":[TD([[makeQuery(id+"F0.imprint","IMPRINT",EDGE,{"derivedFrom":subQ0}),-1.0]])]});}
            var Q117;
            {var subQ0=sQuery(id+"F0.wireOp",EDGE,"E50");Q117=makeQuery(id+"F0.imprint","IMPRINT",FACE,{"disambiguationData":[TD([[makeQuery(id+"F0.imprint","IMPRINT",EDGE,{"derivedFrom":subQ0}),-1.0]])]});}
            var Q118;
            {var subQ0=sQuery(id+"F0.wireOp",EDGE,"E140");Q118=makeQuery(id+"F0.imprint","IMPRINT",FACE,{"disambiguationData":[TD([[makeQuery(id+"F0.imprint","IMPRINT",EDGE,{"derivedFrom":subQ0}),-1.0]])]});}
            var Q119;
            {var subQ0=sQuery(id+"F0.wireOp",EDGE,"E374");Q119=makeQuery(id+"F0.imprint","IMPRINT",FACE,{"disambiguationData":[TD([[makeQuery(id+"F0.imprint","IMPRINT",EDGE,{"derivedFrom":subQ0}),-1.0]])]});}
            var Q120;
            {var subQ0=sQuery(id+"F0.wireOp",EDGE,"E302");Q120=makeQuery(id+"F0.imprint","IMPRINT",FACE,{"disambiguationData":[TD([[makeQuery(id+"F0.imprint","IMPRINT",EDGE,{"derivedFrom":subQ0}),-1.0]])]});}
            extrude(context, id + "F2", {"entities" : qUnion([Q0, Q1, Q2, Q3, Q4, Q5, Q6, Q7, Q8, Q9, Q10, Q11, Q12, Q13, Q14, Q15, Q16, Q17, Q18, Q19, Q20, Q21, Q22, Q23, Q24, Q25, Q26, Q27, Q28, Q29, Q30, Q31, Q32, Q33, Q34, Q35, Q36, Q37, Q38, Q39, Q40, Q41, Q42, Q43, Q44, Q45, Q46, Q47, Q48, Q49, Q50, Q51, Q52, Q53, Q54, Q55, Q56, Q57, Q58, Q59, Q60, Q61, Q62, Q63, Q64, Q65, Q66, Q67, Q68, Q69, Q70, Q71, Q72, Q73, Q74, Q75, Q76, Q77, Q78, Q79, Q80, Q81, Q82, Q83, Q84, Q85, Q86, Q87, Q88, Q89, Q90, Q91, Q92, Q93, Q94, Q95, Q96, Q97, Q98, Q99, Q100, Q101, Q102, Q103, Q104, Q105, Q106, Q107, Q108, Q109, Q110, Q111, Q112, Q113, Q114, Q115, Q116, Q117, Q118, Q119, Q120]), "depth" : 12.7 * mm});
        }
    });
